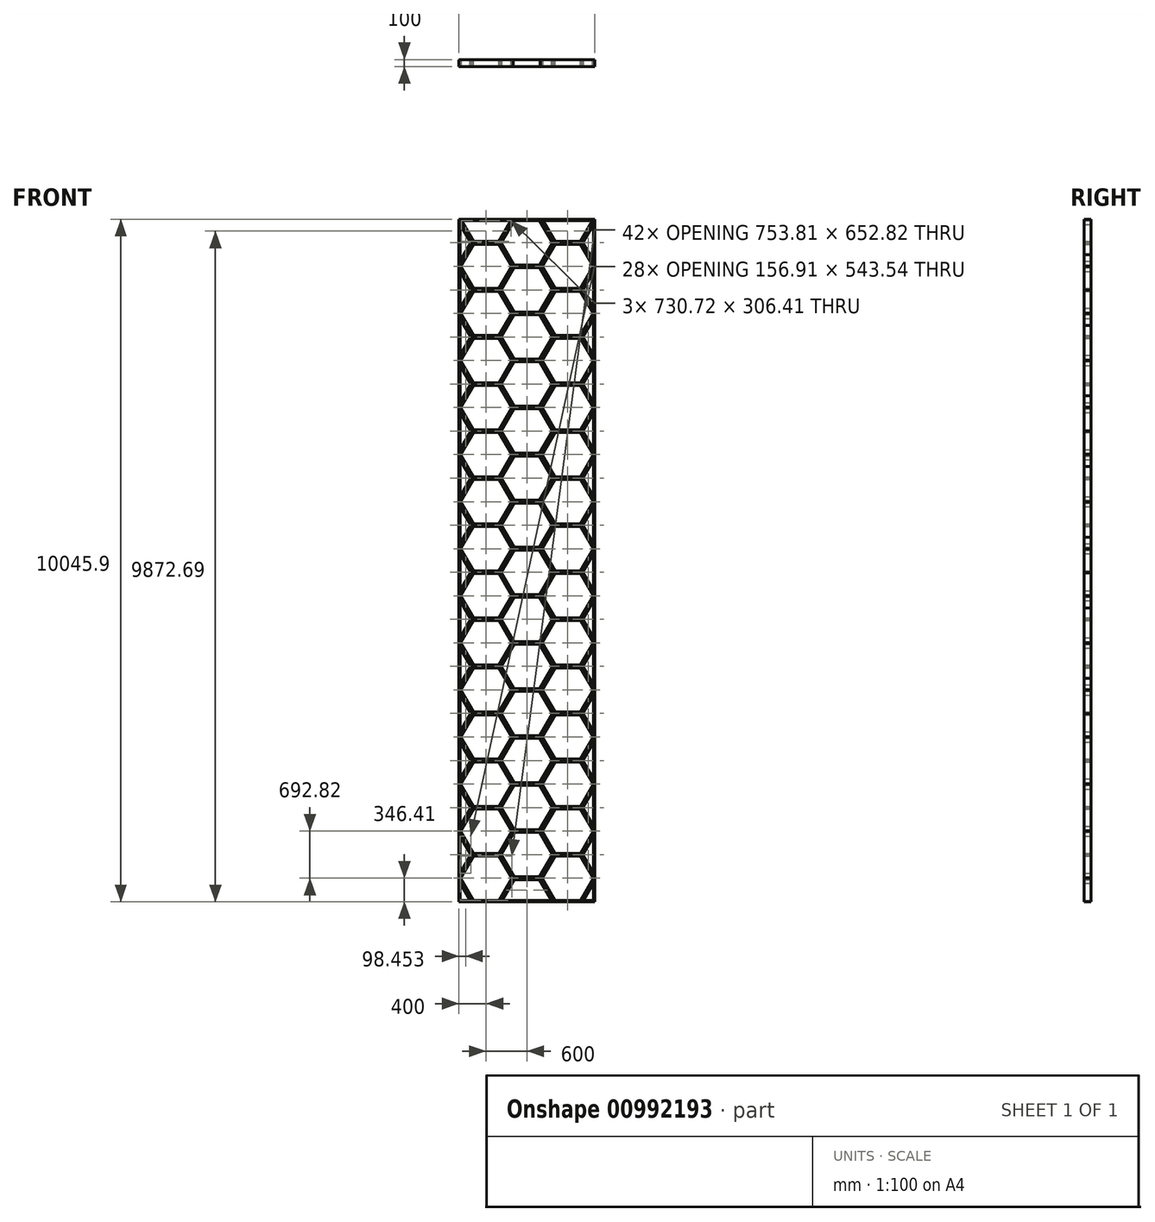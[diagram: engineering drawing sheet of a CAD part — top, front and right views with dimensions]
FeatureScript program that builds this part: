
annotation { "Feature Type Name" : "Feature", "Feature Type Description" : "" }
export const myFeature = defineFeature(function(context is Context, id is Id, definition is map)
    precondition{}
    {
        {
            var Q0;
            Q0=qCreatedBy(makeId("Front.planeOp"),FACE);
            var sketch = newSketch(context, id + "F0", { "sketchPlane" : qUnion([Q0])});
            skLineSegment(sketch, "E0", {"start": v(-200, 346.41) * mm, "end": v(200, 346.41) * mm});
            skLineSegment(sketch, "E1", {"start": v(200, 346.41) * mm, "end": v(400, 0) * mm});
            skLineSegment(sketch, "E2", {"start": v(400, 0) * mm, "end": v(200, -346.41) * mm});
            skLineSegment(sketch, "E3", {"start": v(200, -346.41) * mm, "end": v(-200, -346.41) * mm});
            skLineSegment(sketch, "E4", {"start": v(-200, -346.41) * mm, "end": v(-400, 0) * mm});
            skLineSegment(sketch, "E5", {"start": v(-400, 0) * mm, "end": v(-200, 346.41) * mm});
            skLineSegment(sketch, "E6", {"start": v(-400, 0) * mm, "end": v(-800, 0) * mm});
            skLineSegment(sketch, "E7", {"start": v(-800, 0) * mm, "end": v(-1000, -346.41) * mm});
            skLineSegment(sketch, "E8", {"start": v(-200, -346.41) * mm, "end": v(-1000, -346.41) * mm});
            skLineSegment(sketch, "E9", {"start": v(200, -346.41) * mm, "end": v(400, -346.41) * mm});
            skLineSegment(sketch, "E10", {"start": v(400, -346.41) * mm, "end": v(400, 0) * mm});
            skLineSegment(sketch, "E11", {"start": v(-1000, -346.41) * mm, "end": v(-1400, -346.41) * mm});
            skLineSegment(sketch, "E12", {"start": v(-1400, -346.41) * mm, "end": v(-1600, 0) * mm});
            skLineSegment(sketch, "E13", {"start": v(-1600, 0) * mm, "end": v(-1600, -346.41) * mm});
            skLineSegment(sketch, "E14", {"start": v(-1600, -346.41) * mm, "end": v(-1400, -346.41) * mm});
            skLineSegment(sketch, "E15", {"start": v(-1600, 0) * mm, "end": v(-1400, 346.41) * mm});
            skLineSegment(sketch, "E16", {"start": v(-1400, 346.41) * mm, "end": v(-1000, 346.41) * mm});
            skLineSegment(sketch, "E17", {"start": v(-1000, 346.41) * mm, "end": v(-800, 0) * mm});
            skLineSegment(sketch, "E18", {"start": v(-1400, 346.41) * mm, "end": v(-1600, 692.82) * mm});
            skLineSegment(sketch, "E19", {"start": v(-1600, 692.82) * mm, "end": v(-1600, 0) * mm});
            skLineSegment(sketch, "E20", {"start": v(-1600, 692.82) * mm, "end": v(-1400, 1039.23) * mm});
            skLineSegment(sketch, "E21", {"start": v(-1400, 1039.23) * mm, "end": v(-1000, 1039.23) * mm});
            skLineSegment(sketch, "E22", {"start": v(-1000, 1039.23) * mm, "end": v(-800, 692.82) * mm});
            skLineSegment(sketch, "E23", {"start": v(-800, 692.82) * mm, "end": v(-1000, 346.41) * mm});
            skLineSegment(sketch, "E24", {"start": v(-1400, 1039.23) * mm, "end": v(-1600, 1385.64) * mm});
            skLineSegment(sketch, "E25", {"start": v(-1600, 692.82) * mm, "end": v(-1600, 1385.64) * mm});
            skLineSegment(sketch, "E26", {"start": v(-1600, 1385.64) * mm, "end": v(-1400, 1732.05) * mm});
            skLineSegment(sketch, "E27", {"start": v(-1400, 1732.05) * mm, "end": v(-1600, 2078.46) * mm});
            skLineSegment(sketch, "E28", {"start": v(-1600, 2078.46) * mm, "end": v(-1600, 1385.64) * mm});
            skLineSegment(sketch, "E29", {"start": v(-1600, 2078.46) * mm, "end": v(-1400, 2424.87) * mm});
            skLineSegment(sketch, "E30", {"start": v(-1400, 2424.87) * mm, "end": v(-1600, 2771.28) * mm});
            skLineSegment(sketch, "E31", {"start": v(-1600, 2078.46) * mm, "end": v(-1600, 2771.28) * mm});
            skLineSegment(sketch, "E32.MirrorCS", {"start": v(-1600, 3464.1) * mm, "end": v(-1600, 2771.28) * mm});
            skLineSegment(sketch, "E33.MirrorCS", {"start": v(-1400, 4503.33) * mm, "end": v(-1600, 4156.92) * mm});
            skLineSegment(sketch, "E34.MirrorCS", {"start": v(-1600, 4849.74) * mm, "end": v(-1400, 4503.33) * mm});
            skLineSegment(sketch, "E35.MirrorCS", {"start": v(-1600, 3464.1) * mm, "end": v(-1400, 3117.7) * mm});
            skLineSegment(sketch, "E36.MirrorCS", {"start": v(-1400, 3810.51) * mm, "end": v(-1600, 3464.1) * mm});
            skLineSegment(sketch, "E37.MirrorCS", {"start": v(-1600, 4156.92) * mm, "end": v(-1400, 3810.51) * mm});
            skLineSegment(sketch, "E38.MirrorCS", {"start": v(-1400, 3117.7) * mm, "end": v(-1600, 2771.28) * mm});
            skLineSegment(sketch, "E39.MirrorCS", {"start": v(-1600, 3464.1) * mm, "end": v(-1600, 4156.92) * mm});
            skLineSegment(sketch, "E40", {"start": v(400, 0) * mm, "end": v(400, 9699.48) * mm});
            skLineSegment(sketch, "E41", {"start": v(-200, 346.41) * mm, "end": v(-400, 692.82) * mm});
            skLineSegment(sketch, "E42", {"start": v(-400, 692.82) * mm, "end": v(-800, 692.82) * mm});
            skLineSegment(sketch, "E43", {"start": v(200, 346.41) * mm, "end": v(400, 692.82) * mm});
            skLineSegment(sketch, "E44", {"start": v(400, 692.82) * mm, "end": v(200, 1039.23) * mm});
            skLineSegment(sketch, "E45", {"start": v(200, 1039.23) * mm, "end": v(-200, 1039.23) * mm});
            skLineSegment(sketch, "E46", {"start": v(-200, 1039.23) * mm, "end": v(-400, 692.82) * mm});
            skLineSegment(sketch, "E47", {"start": v(200, 1039.23) * mm, "end": v(400, 1385.64) * mm});
            skLineSegment(sketch, "E48", {"start": v(400, 1385.64) * mm, "end": v(200, 1732.05) * mm});
            skLineSegment(sketch, "E49", {"start": v(200, 1732.05) * mm, "end": v(-200, 1732.05) * mm});
            skLineSegment(sketch, "E50", {"start": v(-200, 1732.05) * mm, "end": v(-400, 1385.64) * mm});
            skLineSegment(sketch, "E51", {"start": v(-400, 1385.64) * mm, "end": v(-800, 1385.64) * mm});
            skLineSegment(sketch, "E52", {"start": v(-800, 1385.64) * mm, "end": v(-1000, 1039.23) * mm});
            skLineSegment(sketch, "E53", {"start": v(-200, 1039.23) * mm, "end": v(-400, 1385.64) * mm});
            skLineSegment(sketch, "E54", {"start": v(-1400, 1732.05) * mm, "end": v(-1000, 1732.05) * mm});
            skLineSegment(sketch, "E55", {"start": v(-1000, 1732.05) * mm, "end": v(-800, 1385.64) * mm});
            skLineSegment(sketch, "E56", {"start": v(400, 2078.46) * mm, "end": v(200, 1732.05) * mm});
            skLineSegment(sketch, "E57", {"start": v(-200, 1732.05) * mm, "end": v(-400, 2078.46) * mm});
            skLineSegment(sketch, "E58", {"start": v(-400, 2078.46) * mm, "end": v(-800, 2078.46) * mm});
            skLineSegment(sketch, "E59", {"start": v(-800, 2078.46) * mm, "end": v(-1000, 1732.05) * mm});
            skLineSegment(sketch, "E60", {"start": v(-1400, 2424.87) * mm, "end": v(-1000, 2424.87) * mm});
            skLineSegment(sketch, "E61", {"start": v(-1000, 2424.87) * mm, "end": v(-800, 2078.46) * mm});
            skLineSegment(sketch, "E62", {"start": v(-400, 2078.46) * mm, "end": v(-200, 2424.87) * mm});
            skLineSegment(sketch, "E63", {"start": v(-200, 2424.87) * mm, "end": v(200, 2424.87) * mm});
            skLineSegment(sketch, "E64", {"start": v(200, 2424.87) * mm, "end": v(400, 2078.46) * mm});
            skLineSegment(sketch, "E65", {"start": v(200, 2424.87) * mm, "end": v(400, 2771.28) * mm});
            skLineSegment(sketch, "E66", {"start": v(400, 2771.28) * mm, "end": v(200, 3117.7) * mm});
            skLineSegment(sketch, "E67", {"start": v(200, 3117.7) * mm, "end": v(400, 3464.1) * mm});
            skLineSegment(sketch, "E68", {"start": v(400, 3464.1) * mm, "end": v(200, 3810.51) * mm});
            skLineSegment(sketch, "E69", {"start": v(200, 3810.51) * mm, "end": v(400, 4156.92) * mm});
            skLineSegment(sketch, "E70", {"start": v(400, 4156.92) * mm, "end": v(200, 4503.33) * mm});
            skLineSegment(sketch, "E71", {"start": v(200, 4503.33) * mm, "end": v(400, 4849.74) * mm});
            skLineSegment(sketch, "E72", {"start": v(400, 4849.74) * mm, "end": v(200, 5196.15) * mm});
            skLineSegment(sketch, "E73", {"start": v(200, 5196.15) * mm, "end": v(400, 5542.56) * mm});
            skLineSegment(sketch, "E74", {"start": v(400, 5542.56) * mm, "end": v(200, 5888.97) * mm});
            skLineSegment(sketch, "E75", {"start": v(200, 5888.97) * mm, "end": v(400, 6235.38) * mm});
            skLineSegment(sketch, "E76", {"start": v(400, 6235.38) * mm, "end": v(200, 6581.8) * mm});
            skLineSegment(sketch, "E77", {"start": v(200, 6581.8) * mm, "end": v(400, 6928.2) * mm});
            skLineSegment(sketch, "E78", {"start": v(400, 6928.2) * mm, "end": v(200, 7274.61) * mm});
            skLineSegment(sketch, "E79", {"start": v(200, 7274.61) * mm, "end": v(400, 7621.02) * mm});
            skLineSegment(sketch, "E80", {"start": v(400, 7621.02) * mm, "end": v(200, 7967.43) * mm});
            skLineSegment(sketch, "E81", {"start": v(200, 7967.43) * mm, "end": v(400, 8313.84) * mm});
            skLineSegment(sketch, "E82", {"start": v(400, 8313.84) * mm, "end": v(200, 8660.25) * mm});
            skLineSegment(sketch, "E83", {"start": v(200, 8660.25) * mm, "end": v(400, 9006.66) * mm});
            skLineSegment(sketch, "E84", {"start": v(400, 9006.66) * mm, "end": v(200, 9353.07) * mm});
            skLineSegment(sketch, "E85", {"start": v(-1600, 4156.92) * mm, "end": v(-1600, 4849.74) * mm});
            skLineSegment(sketch, "E86", {"start": v(-1600, 4849.74) * mm, "end": v(-1600, 9699.48) * mm});
            skLineSegment(sketch, "E87", {"start": v(-1600, 4849.74) * mm, "end": v(-1400, 5196.15) * mm});
            skLineSegment(sketch, "E88", {"start": v(-1400, 5196.15) * mm, "end": v(-1600, 5542.56) * mm});
            skLineSegment(sketch, "E89", {"start": v(-1400, 5196.15) * mm, "end": v(-1000, 5196.15) * mm});
            skLineSegment(sketch, "E90", {"start": v(-1000, 5196.15) * mm, "end": v(-800, 4849.74) * mm});
            skLineSegment(sketch, "E91", {"start": v(-800, 4849.74) * mm, "end": v(-1000, 4503.33) * mm});
            skLineSegment(sketch, "E92", {"start": v(-1000, 4503.33) * mm, "end": v(-1400, 4503.33) * mm});
            skLineSegment(sketch, "E93", {"start": v(-1600, 5542.56) * mm, "end": v(-1400, 5888.97) * mm});
            skLineSegment(sketch, "E94", {"start": v(-1400, 5888.97) * mm, "end": v(-1600, 6235.38) * mm});
            skLineSegment(sketch, "E95", {"start": v(-1600, 6235.38) * mm, "end": v(-1400, 6581.8) * mm});
            skLineSegment(sketch, "E96", {"start": v(-1400, 6581.8) * mm, "end": v(-1600, 6928.2) * mm});
            skLineSegment(sketch, "E97", {"start": v(-1600, 6928.2) * mm, "end": v(-1400, 7274.61) * mm});
            skLineSegment(sketch, "E98", {"start": v(-1400, 7274.61) * mm, "end": v(-1600, 7621.02) * mm});
            skLineSegment(sketch, "E99", {"start": v(-1600, 7621.02) * mm, "end": v(-1400, 7967.43) * mm});
            skLineSegment(sketch, "E100", {"start": v(-1400, 7967.43) * mm, "end": v(-1600, 8313.84) * mm});
            skLineSegment(sketch, "E101", {"start": v(-1600, 8313.84) * mm, "end": v(-1400, 8660.25) * mm});
            skLineSegment(sketch, "E102", {"start": v(-1400, 8660.25) * mm, "end": v(-1600, 9006.66) * mm});
            skLineSegment(sketch, "E103", {"start": v(200, 9353.07) * mm, "end": v(400, 9699.48) * mm});
            skLineSegment(sketch, "E104", {"start": v(-1600, 9006.66) * mm, "end": v(-1400, 9353.07) * mm});
            skLineSegment(sketch, "E105", {"start": v(-1400, 9353.07) * mm, "end": v(-1600, 9699.48) * mm});
            skLineSegment(sketch, "E106", {"start": v(-1600, 9699.48) * mm, "end": v(400, 9699.48) * mm});
            skLineSegment(sketch, "E107", {"start": v(-200, 2424.87) * mm, "end": v(-400, 2771.28) * mm});
            skLineSegment(sketch, "E108", {"start": v(-400, 2771.28) * mm, "end": v(-200, 3117.7) * mm});
            skLineSegment(sketch, "E109", {"start": v(-200, 3117.7) * mm, "end": v(200, 3117.7) * mm});
            skLineSegment(sketch, "E110", {"start": v(-400, 2771.28) * mm, "end": v(-800, 2771.28) * mm});
            skLineSegment(sketch, "E111", {"start": v(-800, 2771.28) * mm, "end": v(-1000, 2424.87) * mm});
            skLineSegment(sketch, "E112", {"start": v(-1400, 3117.7) * mm, "end": v(-1000, 3117.7) * mm});
            skLineSegment(sketch, "E113", {"start": v(-1000, 3117.7) * mm, "end": v(-800, 2771.28) * mm});
            skLineSegment(sketch, "E114", {"start": v(-1400, 3810.51) * mm, "end": v(-1000, 3810.51) * mm});
            skLineSegment(sketch, "E115", {"start": v(-1000, 3810.51) * mm, "end": v(-800, 3464.1) * mm});
            skLineSegment(sketch, "E116", {"start": v(-800, 3464.1) * mm, "end": v(-1000, 3117.7) * mm});
            skLineSegment(sketch, "E117", {"start": v(-200, 3117.7) * mm, "end": v(-400, 3464.1) * mm});
            skLineSegment(sketch, "E118", {"start": v(-400, 3464.1) * mm, "end": v(-800, 3464.1) * mm});
            skLineSegment(sketch, "E119", {"start": v(-400, 3464.1) * mm, "end": v(-200, 3810.51) * mm});
            skLineSegment(sketch, "E120", {"start": v(-200, 3810.51) * mm, "end": v(200, 3810.51) * mm});
            skLineSegment(sketch, "E121", {"start": v(-1000, 3810.51) * mm, "end": v(-800, 4156.92) * mm});
            skLineSegment(sketch, "E122", {"start": v(-800, 4156.92) * mm, "end": v(-1000, 4503.33) * mm});
            skLineSegment(sketch, "E123", {"start": v(-800, 4849.74) * mm, "end": v(-400, 4849.74) * mm});
            skLineSegment(sketch, "E124", {"start": v(-400, 4849.74) * mm, "end": v(-200, 4503.33) * mm});
            skLineSegment(sketch, "E125", {"start": v(-200, 4503.33) * mm, "end": v(-400, 4156.92) * mm});
            skLineSegment(sketch, "E126", {"start": v(-400, 4156.92) * mm, "end": v(-800, 4156.92) * mm});
            skLineSegment(sketch, "E127", {"start": v(-400, 4156.92) * mm, "end": v(-200, 3810.51) * mm});
            skLineSegment(sketch, "E128", {"start": v(200, 4503.33) * mm, "end": v(-200, 4503.33) * mm});
            skLineSegment(sketch, "E129", {"start": v(-400, 4849.74) * mm, "end": v(-200, 5196.15) * mm});
            skLineSegment(sketch, "E130", {"start": v(-200, 5196.15) * mm, "end": v(200, 5196.15) * mm});
            skLineSegment(sketch, "E131", {"start": v(200, 5888.97) * mm, "end": v(-200, 5888.97) * mm});
            skLineSegment(sketch, "E132", {"start": v(-200, 5888.97) * mm, "end": v(-400, 5542.56) * mm});
            skLineSegment(sketch, "E133", {"start": v(-400, 5542.56) * mm, "end": v(-200, 5196.15) * mm});
            skLineSegment(sketch, "E134", {"start": v(-1000, 5196.15) * mm, "end": v(-800, 5542.56) * mm});
            skLineSegment(sketch, "E135", {"start": v(-800, 5542.56) * mm, "end": v(-400, 5542.56) * mm});
            skLineSegment(sketch, "E136", {"start": v(-1400, 5888.97) * mm, "end": v(-1000, 5888.97) * mm});
            skLineSegment(sketch, "E137", {"start": v(-1000, 5888.97) * mm, "end": v(-800, 5542.56) * mm});
            skLineSegment(sketch, "E138", {"start": v(-1000, 5888.97) * mm, "end": v(-800, 6235.38) * mm});
            skLineSegment(sketch, "E139", {"start": v(-800, 6235.38) * mm, "end": v(-400, 6235.38) * mm});
            skLineSegment(sketch, "E140", {"start": v(-400, 6235.38) * mm, "end": v(-200, 5888.97) * mm});
            skLineSegment(sketch, "E141", {"start": v(200, 6581.8) * mm, "end": v(-200, 6581.8) * mm});
            skLineSegment(sketch, "E142", {"start": v(-200, 6581.8) * mm, "end": v(-400, 6235.38) * mm});
            skLineSegment(sketch, "E143", {"start": v(-800, 6235.38) * mm, "end": v(-1000, 6581.8) * mm});
            skLineSegment(sketch, "E144", {"start": v(-1000, 6581.8) * mm, "end": v(-1400, 6581.8) * mm});
            skLineSegment(sketch, "E145", {"start": v(-1400, 7274.61) * mm, "end": v(-1000, 7274.61) * mm});
            skLineSegment(sketch, "E146", {"start": v(-1000, 7274.61) * mm, "end": v(-800, 6928.2) * mm});
            skLineSegment(sketch, "E147", {"start": v(-800, 6928.2) * mm, "end": v(-400, 6928.2) * mm});
            skLineSegment(sketch, "E148", {"start": v(-400, 6928.2) * mm, "end": v(-200, 7274.61) * mm});
            skLineSegment(sketch, "E149", {"start": v(-200, 7274.61) * mm, "end": v(200, 7274.61) * mm});
            skLineSegment(sketch, "E150", {"start": v(-400, 6928.2) * mm, "end": v(-200, 6581.8) * mm});
            skLineSegment(sketch, "E151", {"start": v(-800, 6928.2) * mm, "end": v(-1000, 6581.8) * mm});
            skLineSegment(sketch, "E152", {"start": v(-200, 7274.61) * mm, "end": v(-400, 7621.02) * mm});
            skLineSegment(sketch, "E153", {"start": v(-400, 7621.02) * mm, "end": v(-200, 7967.43) * mm});
            skLineSegment(sketch, "E154", {"start": v(-200, 7967.43) * mm, "end": v(200, 7967.43) * mm});
            skLineSegment(sketch, "E155", {"start": v(-400, 7621.02) * mm, "end": v(-800, 7621.02) * mm});
            skLineSegment(sketch, "E156", {"start": v(-800, 7621.02) * mm, "end": v(-1000, 7274.61) * mm});
            skLineSegment(sketch, "E157", {"start": v(-1400, 7967.43) * mm, "end": v(-1000, 7967.43) * mm});
            skLineSegment(sketch, "E158", {"start": v(-1000, 7967.43) * mm, "end": v(-800, 7621.02) * mm});
            skLineSegment(sketch, "E159", {"start": v(-1400, 8660.25) * mm, "end": v(-1000, 8660.25) * mm});
            skLineSegment(sketch, "E160", {"start": v(-1000, 8660.25) * mm, "end": v(-800, 8313.84) * mm});
            skLineSegment(sketch, "E161", {"start": v(-800, 8313.84) * mm, "end": v(-1000, 7967.43) * mm});
            skLineSegment(sketch, "E162", {"start": v(-200, 7967.43) * mm, "end": v(-400, 8313.84) * mm});
            skLineSegment(sketch, "E163", {"start": v(-400, 8313.84) * mm, "end": v(-800, 8313.84) * mm});
            skLineSegment(sketch, "E164", {"start": v(-400, 8313.84) * mm, "end": v(-200, 8660.25) * mm});
            skLineSegment(sketch, "E165", {"start": v(-200, 8660.25) * mm, "end": v(200, 8660.25) * mm});
            skLineSegment(sketch, "E166", {"start": v(-200, 8660.25) * mm, "end": v(-400, 9006.66) * mm});
            skLineSegment(sketch, "E167", {"start": v(-400, 9006.66) * mm, "end": v(-800, 9006.66) * mm});
            skLineSegment(sketch, "E168", {"start": v(-800, 9006.66) * mm, "end": v(-1000, 8660.25) * mm});
            skLineSegment(sketch, "E169", {"start": v(-1400, 9353.07) * mm, "end": v(-1000, 9353.07) * mm});
            skLineSegment(sketch, "E170", {"start": v(-1000, 9353.07) * mm, "end": v(-800, 9006.66) * mm});
            skLineSegment(sketch, "E171", {"start": v(-400, 9006.66) * mm, "end": v(-200, 9353.07) * mm});
            skLineSegment(sketch, "E172", {"start": v(-200, 9353.07) * mm, "end": v(200, 9353.07) * mm});
            skLineSegment(sketch, "E173", {"start": v(-200, 9353.07) * mm, "end": v(-400, 9699.48) * mm});
            skLineSegment(sketch, "E174", {"start": v(-1000, 9353.07) * mm, "end": v(-800, 9699.48) * mm});
            skPoint(sketch, "E175", {"position": v(400, 9179.48) * mm});
            skPoint(sketch, "E176", {"position": v(400, 8659.48) * mm});
            skPoint(sketch, "E177", {"position": v(400, 8139.48) * mm});
            skPoint(sketch, "E178", {"position": v(400, 7619.48) * mm});
            skPoint(sketch, "E179", {"position": v(400, 7099.48) * mm});
            skPoint(sketch, "E180", {"position": v(400, 6579.48) * mm});
            skPoint(sketch, "E181", {"position": v(400, 6059.48) * mm});
            skPoint(sketch, "E182", {"position": v(400, 5539.48) * mm});
            skPoint(sketch, "E183", {"position": v(400, 5019.48) * mm});
            skPoint(sketch, "E184", {"position": v(400, 4499.48) * mm});
            skPoint(sketch, "E185", {"position": v(400, 3979.48) * mm});
            skPoint(sketch, "E186", {"position": v(400, 3459.48) * mm});
            skPoint(sketch, "E187", {"position": v(400, 2939.48) * mm});
            skPoint(sketch, "E188", {"position": v(400, 2419.48) * mm});
            skPoint(sketch, "E189", {"position": v(400, 1899.48) * mm});
            skPoint(sketch, "E190", {"position": v(400, 1379.48) * mm});
            skPoint(sketch, "E191", {"position": v(400, -173.2) * mm});
            skPoint(sketch, "E192", {"position": v(400, 859.48) * mm});
            skPoint(sketch, "E193", {"position": v(400, 339.48) * mm});
            skSolve(sketch);
        }
        {
            var Q0;
            Q0=makeQuery(id+"F0.imprint","IMPRINT",FACE,{"disambiguationData":[TD([[makeQuery(id+"F0.imprint","IMPRINT",EDGE,{"derivedFrom":sQuery(id+"F0.wireOp",EDGE,"E153")}),1.0]])]});
            var Q1;
            Q1=makeQuery(id+"F0.imprint","IMPRINT",FACE,{"disambiguationData":[TD([[makeQuery(id+"F0.imprint","IMPRINT",EDGE,{"derivedFrom":sQuery(id+"F0.wireOp",EDGE,"E22")}),1.0]])]});
            var Q2;
            Q2=makeQuery(id+"F0.imprint","IMPRINT",FACE,{"disambiguationData":[TD([[makeQuery(id+"F0.imprint","IMPRINT",EDGE,{"derivedFrom":sQuery(id+"F0.wireOp",EDGE,"E58")}),-1.0]])]});
            var Q3;
            Q3=makeQuery(id+"F0.imprint","IMPRINT",FACE,{"disambiguationData":[TD([[makeQuery(id+"F0.imprint","IMPRINT",EDGE,{"derivedFrom":sQuery(id+"F0.wireOp",EDGE,"E115")}),1.0]])]});
            var Q4;
            Q4=makeQuery(id+"F0.imprint","IMPRINT",FACE,{"disambiguationData":[TD([[makeQuery(id+"F0.imprint","IMPRINT",EDGE,{"derivedFrom":sQuery(id+"F0.wireOp",EDGE,"E90")}),1.0]])]});
            var Q5;
            Q5=makeQuery(id+"F0.imprint","IMPRINT",FACE,{"disambiguationData":[TD([[makeQuery(id+"F0.imprint","IMPRINT",EDGE,{"derivedFrom":sQuery(id+"F0.wireOp",EDGE,"E139")}),1.0]])]});
            var Q6;
            Q6=makeQuery(id+"F0.imprint","IMPRINT",FACE,{"disambiguationData":[TD([[makeQuery(id+"F0.imprint","IMPRINT",EDGE,{"derivedFrom":sQuery(id+"F0.wireOp",EDGE,"E2")}),1.0]])]});
            var Q7;
            Q7=makeQuery(id+"F0.imprint","IMPRINT",FACE,{"disambiguationData":[TD([[makeQuery(id+"F0.imprint","IMPRINT",EDGE,{"derivedFrom":sQuery(id+"F0.wireOp",EDGE,"E12")}),1.0]])]});
            var Q8;
            {var subQ0=sQuery(id+"F0.wireOp",EDGE,"E1");Q8=makeQuery(id+"F0.imprint","IMPRINT",FACE,{"disambiguationData":[TD([[makeQuery(id+"F0.imprint","IMPRINT",EDGE,{"derivedFrom":subQ0}),1.0]])]});}
            var Q9;
            Q9=makeQuery(id+"F0.imprint","IMPRINT",FACE,{"disambiguationData":[TD([[makeQuery(id+"F0.imprint","IMPRINT",EDGE,{"derivedFrom":sQuery(id+"F0.wireOp",EDGE,"E15")}),1.0]])]});
            var Q10;
            Q10=makeQuery(id+"F0.imprint","IMPRINT",FACE,{"disambiguationData":[TD([[makeQuery(id+"F0.imprint","IMPRINT",EDGE,{"derivedFrom":sQuery(id+"F0.wireOp",EDGE,"E20")}),1.0]])]});
            var Q11;
            Q11=makeQuery(id+"F0.imprint","IMPRINT",FACE,{"disambiguationData":[TD([[makeQuery(id+"F0.imprint","IMPRINT",EDGE,{"derivedFrom":sQuery(id+"F0.wireOp",EDGE,"E26")}),1.0]])]});
            var Q12;
            Q12=makeQuery(id+"F0.imprint","IMPRINT",FACE,{"disambiguationData":[TD([[makeQuery(id+"F0.imprint","IMPRINT",EDGE,{"derivedFrom":sQuery(id+"F0.wireOp",EDGE,"E29")}),1.0]])]});
            var Q13;
            Q13=makeQuery(id+"F0.imprint","IMPRINT",FACE,{"disambiguationData":[TD([[makeQuery(id+"F0.imprint","IMPRINT",EDGE,{"derivedFrom":sQuery(id+"F0.wireOp",EDGE,"E32.MirrorCS")}),1.0]])]});
            var Q14;
            Q14=makeQuery(id+"F0.imprint","IMPRINT",FACE,{"disambiguationData":[TD([[makeQuery(id+"F0.imprint","IMPRINT",EDGE,{"derivedFrom":sQuery(id+"F0.wireOp",EDGE,"E33.MirrorCS")}),-1.0]])]});
            var Q15;
            Q15=makeQuery(id+"F0.imprint","IMPRINT",FACE,{"disambiguationData":[TD([[makeQuery(id+"F0.imprint","IMPRINT",EDGE,{"derivedFrom":sQuery(id+"F0.wireOp",EDGE,"E36.MirrorCS")}),-1.0]])]});
            var Q16;
            {var subQ0=sQuery(id+"F0.wireOp",EDGE,"E44");Q16=makeQuery(id+"F0.imprint","IMPRINT",FACE,{"disambiguationData":[TD([[makeQuery(id+"F0.imprint","IMPRINT",EDGE,{"derivedFrom":subQ0}),-1.0]])]});}
            var Q17;
            {var subQ0=sQuery(id+"F0.wireOp",EDGE,"E48");Q17=makeQuery(id+"F0.imprint","IMPRINT",FACE,{"disambiguationData":[TD([[makeQuery(id+"F0.imprint","IMPRINT",EDGE,{"derivedFrom":subQ0}),-1.0]])]});}
            var Q18;
            {var subQ0=sQuery(id+"F0.wireOp",EDGE,"E64");Q18=makeQuery(id+"F0.imprint","IMPRINT",FACE,{"disambiguationData":[TD([[makeQuery(id+"F0.imprint","IMPRINT",EDGE,{"derivedFrom":subQ0}),1.0]])]});}
            var Q19;
            {var subQ0=sQuery(id+"F0.wireOp",EDGE,"E66");Q19=makeQuery(id+"F0.imprint","IMPRINT",FACE,{"disambiguationData":[TD([[makeQuery(id+"F0.imprint","IMPRINT",EDGE,{"derivedFrom":subQ0}),-1.0]])]});}
            var Q20;
            {var subQ0=sQuery(id+"F0.wireOp",EDGE,"E68");Q20=makeQuery(id+"F0.imprint","IMPRINT",FACE,{"disambiguationData":[TD([[makeQuery(id+"F0.imprint","IMPRINT",EDGE,{"derivedFrom":subQ0}),-1.0]])]});}
            var Q21;
            {var subQ0=sQuery(id+"F0.wireOp",EDGE,"E70");Q21=makeQuery(id+"F0.imprint","IMPRINT",FACE,{"disambiguationData":[TD([[makeQuery(id+"F0.imprint","IMPRINT",EDGE,{"derivedFrom":subQ0}),-1.0]])]});}
            var Q22;
            {var subQ0=sQuery(id+"F0.wireOp",EDGE,"E72");Q22=makeQuery(id+"F0.imprint","IMPRINT",FACE,{"disambiguationData":[TD([[makeQuery(id+"F0.imprint","IMPRINT",EDGE,{"derivedFrom":subQ0}),-1.0]])]});}
            var Q23;
            {var subQ0=sQuery(id+"F0.wireOp",EDGE,"E74");Q23=makeQuery(id+"F0.imprint","IMPRINT",FACE,{"disambiguationData":[TD([[makeQuery(id+"F0.imprint","IMPRINT",EDGE,{"derivedFrom":subQ0}),-1.0]])]});}
            var Q24;
            {var subQ0=sQuery(id+"F0.wireOp",EDGE,"E76");Q24=makeQuery(id+"F0.imprint","IMPRINT",FACE,{"disambiguationData":[TD([[makeQuery(id+"F0.imprint","IMPRINT",EDGE,{"derivedFrom":subQ0}),-1.0]])]});}
            var Q25;
            {var subQ0=sQuery(id+"F0.wireOp",EDGE,"E78");Q25=makeQuery(id+"F0.imprint","IMPRINT",FACE,{"disambiguationData":[TD([[makeQuery(id+"F0.imprint","IMPRINT",EDGE,{"derivedFrom":subQ0}),-1.0]])]});}
            var Q26;
            {var subQ0=sQuery(id+"F0.wireOp",EDGE,"E80");Q26=makeQuery(id+"F0.imprint","IMPRINT",FACE,{"disambiguationData":[TD([[makeQuery(id+"F0.imprint","IMPRINT",EDGE,{"derivedFrom":subQ0}),-1.0]])]});}
            var Q27;
            {var subQ0=sQuery(id+"F0.wireOp",EDGE,"E82");Q27=makeQuery(id+"F0.imprint","IMPRINT",FACE,{"disambiguationData":[TD([[makeQuery(id+"F0.imprint","IMPRINT",EDGE,{"derivedFrom":subQ0}),-1.0]])]});}
            var Q28;
            {var subQ2=sQuery(id+"F0.wireOp",EDGE,"E84");Q28=makeQuery(id+"F0.imprint","IMPRINT",FACE,{"disambiguationData":[TD([[makeQuery(id+"F0.imprint","IMPRINT",EDGE,{"derivedFrom":subQ2}),-1.0]])]});}
            var Q29;
            {var subQ0=sQuery(id+"F0.wireOp",EDGE,"E87");Q29=makeQuery(id+"F0.imprint","IMPRINT",FACE,{"disambiguationData":[TD([[makeQuery(id+"F0.imprint","IMPRINT",EDGE,{"derivedFrom":subQ0}),1.0]])]});}
            var Q30;
            {var subQ0=sQuery(id+"F0.wireOp",EDGE,"E93");Q30=makeQuery(id+"F0.imprint","IMPRINT",FACE,{"disambiguationData":[TD([[makeQuery(id+"F0.imprint","IMPRINT",EDGE,{"derivedFrom":subQ0}),1.0]])]});}
            var Q31;
            {var subQ0=sQuery(id+"F0.wireOp",EDGE,"E95");Q31=makeQuery(id+"F0.imprint","IMPRINT",FACE,{"disambiguationData":[TD([[makeQuery(id+"F0.imprint","IMPRINT",EDGE,{"derivedFrom":subQ0}),1.0]])]});}
            var Q32;
            {var subQ0=sQuery(id+"F0.wireOp",EDGE,"E97");Q32=makeQuery(id+"F0.imprint","IMPRINT",FACE,{"disambiguationData":[TD([[makeQuery(id+"F0.imprint","IMPRINT",EDGE,{"derivedFrom":subQ0}),1.0]])]});}
            var Q33;
            {var subQ0=sQuery(id+"F0.wireOp",EDGE,"E99");Q33=makeQuery(id+"F0.imprint","IMPRINT",FACE,{"disambiguationData":[TD([[makeQuery(id+"F0.imprint","IMPRINT",EDGE,{"derivedFrom":subQ0}),1.0]])]});}
            var Q34;
            {var subQ0=sQuery(id+"F0.wireOp",EDGE,"E101");Q34=makeQuery(id+"F0.imprint","IMPRINT",FACE,{"disambiguationData":[TD([[makeQuery(id+"F0.imprint","IMPRINT",EDGE,{"derivedFrom":subQ0}),1.0]])]});}
            var Q35;
            {var subQ2=sQuery(id+"F0.wireOp",EDGE,"E104");Q35=makeQuery(id+"F0.imprint","IMPRINT",FACE,{"disambiguationData":[TD([[makeQuery(id+"F0.imprint","IMPRINT",EDGE,{"derivedFrom":subQ2}),1.0]])]});}
            var Q36;
            Q36=makeQuery(id+"F0.imprint","IMPRINT",FACE,{"disambiguationData":[TD([[makeQuery(id+"F0.imprint","IMPRINT",EDGE,{"derivedFrom":sQuery(id+"F0.wireOp",EDGE,"E4")}),1.0]])]});
            var Q37;
            Q37=makeQuery(id+"F0.imprint","IMPRINT",FACE,{"disambiguationData":[TD([[makeQuery(id+"F0.imprint","IMPRINT",EDGE,{"derivedFrom":sQuery(id+"F0.wireOp",EDGE,"E167")}),-1.0]])]});
            extrude(context, id + "F1", {"entities" : qUnion([Q0, Q1, Q2, Q3, Q4, Q5, Q6, Q7, Q8, Q9, Q10, Q11, Q12, Q13, Q14, Q15, Q16, Q17, Q18, Q19, Q20, Q21, Q22, Q23, Q24, Q25, Q26, Q27, Q28, Q29, Q30, Q31, Q32, Q33, Q34, Q35, Q36, Q37]), "depth" : 100 * mm, "offsetDistance" : 25 * mm});
        }
        {
            var Q0;
            Q0=makeQuery(id+"F1.opExtrude","CAP_FACE",FACE,{"disambiguationData":[OSD([sQuery(id+"F0.wireOp",EDGE,"E106"),sQuery(id+"F0.wireOp",EDGE,"E167"),sQuery(id+"F0.wireOp",EDGE,"E170"),sQuery(id+"F0.wireOp",EDGE,"E171"),sQuery(id+"F0.wireOp",EDGE,"E173"),sQuery(id+"F0.wireOp",EDGE,"E174")])],"isStart":false});
            var Q1;
            Q1=makeQuery(id+"F1.opExtrude","CAP_FACE",FACE,{"disambiguationData":[OSD([sQuery(id+"F0.wireOp",EDGE,"E86"),sQuery(id+"F0.wireOp",EDGE,"E104"),sQuery(id+"F0.wireOp",EDGE,"E105")])],"isStart":false});
            var Q2;
            Q2=makeQuery(id+"F1.opExtrude","CAP_FACE",FACE,{"disambiguationData":[OSD([sQuery(id+"F0.wireOp",EDGE,"E86"),sQuery(id+"F0.wireOp",EDGE,"E101"),sQuery(id+"F0.wireOp",EDGE,"E102")])],"isStart":false});
            var Q3;
            Q3=makeQuery(id+"F1.opExtrude","CAP_FACE",FACE,{"disambiguationData":[OSD([sQuery(id+"F0.wireOp",EDGE,"E86"),sQuery(id+"F0.wireOp",EDGE,"E99"),sQuery(id+"F0.wireOp",EDGE,"E100")])],"isStart":false});
            var Q4;
            Q4=makeQuery(id+"F1.opExtrude","CAP_FACE",FACE,{"disambiguationData":[OSD([sQuery(id+"F0.wireOp",EDGE,"E86"),sQuery(id+"F0.wireOp",EDGE,"E97"),sQuery(id+"F0.wireOp",EDGE,"E98")])],"isStart":false});
            var Q5;
            Q5=makeQuery(id+"F1.opExtrude","CAP_FACE",FACE,{"disambiguationData":[OSD([sQuery(id+"F0.wireOp",EDGE,"E86"),sQuery(id+"F0.wireOp",EDGE,"E95"),sQuery(id+"F0.wireOp",EDGE,"E96")])],"isStart":false});
            var Q6;
            Q6=makeQuery(id+"F1.opExtrude","CAP_FACE",FACE,{"disambiguationData":[OSD([sQuery(id+"F0.wireOp",EDGE,"E86"),sQuery(id+"F0.wireOp",EDGE,"E93"),sQuery(id+"F0.wireOp",EDGE,"E94")])],"isStart":false});
            var Q7;
            Q7=makeQuery(id+"F1.opExtrude","CAP_FACE",FACE,{"disambiguationData":[OSD([sQuery(id+"F0.wireOp",EDGE,"E86"),sQuery(id+"F0.wireOp",EDGE,"E87"),sQuery(id+"F0.wireOp",EDGE,"E88")])],"isStart":false});
            var Q8;
            Q8=makeQuery(id+"F1.opExtrude","CAP_FACE",FACE,{"disambiguationData":[OSD([sQuery(id+"F0.wireOp",EDGE,"E33.MirrorCS"),sQuery(id+"F0.wireOp",EDGE,"E34.MirrorCS"),sQuery(id+"F0.wireOp",EDGE,"E85")])],"isStart":false});
            var Q9;
            Q9=makeQuery(id+"F1.opExtrude","CAP_FACE",FACE,{"disambiguationData":[OSD([sQuery(id+"F0.wireOp",EDGE,"E36.MirrorCS"),sQuery(id+"F0.wireOp",EDGE,"E37.MirrorCS"),sQuery(id+"F0.wireOp",EDGE,"E39.MirrorCS")])],"isStart":false});
            var Q10;
            Q10=makeQuery(id+"F1.opExtrude","CAP_FACE",FACE,{"disambiguationData":[OSD([sQuery(id+"F0.wireOp",EDGE,"E32.MirrorCS"),sQuery(id+"F0.wireOp",EDGE,"E35.MirrorCS"),sQuery(id+"F0.wireOp",EDGE,"E38.MirrorCS")])],"isStart":false});
            var Q11;
            Q11=makeQuery(id+"F1.opExtrude","CAP_FACE",FACE,{"disambiguationData":[OSD([sQuery(id+"F0.wireOp",EDGE,"E29"),sQuery(id+"F0.wireOp",EDGE,"E30"),sQuery(id+"F0.wireOp",EDGE,"E31")])],"isStart":false});
            var Q12;
            Q12=makeQuery(id+"F1.opExtrude","CAP_FACE",FACE,{"disambiguationData":[OSD([sQuery(id+"F0.wireOp",EDGE,"E26"),sQuery(id+"F0.wireOp",EDGE,"E27"),sQuery(id+"F0.wireOp",EDGE,"E28")])],"isStart":false});
            var Q13;
            Q13=makeQuery(id+"F1.opExtrude","CAP_FACE",FACE,{"disambiguationData":[OSD([sQuery(id+"F0.wireOp",EDGE,"E20"),sQuery(id+"F0.wireOp",EDGE,"E24"),sQuery(id+"F0.wireOp",EDGE,"E25")])],"isStart":false});
            var Q14;
            Q14=makeQuery(id+"F1.opExtrude","CAP_FACE",FACE,{"disambiguationData":[OSD([sQuery(id+"F0.wireOp",EDGE,"E15"),sQuery(id+"F0.wireOp",EDGE,"E18"),sQuery(id+"F0.wireOp",EDGE,"E19")])],"isStart":false});
            var Q15;
            Q15=makeQuery(id+"F1.opExtrude","CAP_FACE",FACE,{"disambiguationData":[OSD([sQuery(id+"F0.wireOp",EDGE,"E12"),sQuery(id+"F0.wireOp",EDGE,"E13"),sQuery(id+"F0.wireOp",EDGE,"E14")])],"isStart":false});
            var Q16;
            Q16=makeQuery(id+"F1.opExtrude","CAP_FACE",FACE,{"disambiguationData":[OSD([sQuery(id+"F0.wireOp",EDGE,"E4"),sQuery(id+"F0.wireOp",EDGE,"E6"),sQuery(id+"F0.wireOp",EDGE,"E7"),sQuery(id+"F0.wireOp",EDGE,"E8")])],"isStart":false});
            var Q17;
            Q17=makeQuery(id+"F1.opExtrude","CAP_FACE",FACE,{"disambiguationData":[OSD([sQuery(id+"F0.wireOp",EDGE,"E2"),sQuery(id+"F0.wireOp",EDGE,"E9"),sQuery(id+"F0.wireOp",EDGE,"E10")])],"isStart":false});
            var Q18;
            Q18=makeQuery(id+"F1.opExtrude","CAP_FACE",FACE,{"disambiguationData":[OSD([sQuery(id+"F0.wireOp",EDGE,"E1"),sQuery(id+"F0.wireOp",EDGE,"E40"),sQuery(id+"F0.wireOp",EDGE,"E43")])],"isStart":false});
            var Q19;
            Q19=makeQuery(id+"F1.opExtrude","CAP_FACE",FACE,{"disambiguationData":[OSD([sQuery(id+"F0.wireOp",EDGE,"E40"),sQuery(id+"F0.wireOp",EDGE,"E44"),sQuery(id+"F0.wireOp",EDGE,"E47")])],"isStart":false});
            var Q20;
            Q20=makeQuery(id+"F1.opExtrude","CAP_FACE",FACE,{"disambiguationData":[OSD([sQuery(id+"F0.wireOp",EDGE,"E40"),sQuery(id+"F0.wireOp",EDGE,"E48"),sQuery(id+"F0.wireOp",EDGE,"E56")])],"isStart":false});
            var Q21;
            Q21=makeQuery(id+"F1.opExtrude","CAP_FACE",FACE,{"disambiguationData":[OSD([sQuery(id+"F0.wireOp",EDGE,"E22"),sQuery(id+"F0.wireOp",EDGE,"E42"),sQuery(id+"F0.wireOp",EDGE,"E46"),sQuery(id+"F0.wireOp",EDGE,"E51"),sQuery(id+"F0.wireOp",EDGE,"E52"),sQuery(id+"F0.wireOp",EDGE,"E53")])],"isStart":false});
            var Q22;
            Q22=makeQuery(id+"F1.opExtrude","CAP_FACE",FACE,{"disambiguationData":[OSD([sQuery(id+"F0.wireOp",EDGE,"E58"),sQuery(id+"F0.wireOp",EDGE,"E61"),sQuery(id+"F0.wireOp",EDGE,"E62"),sQuery(id+"F0.wireOp",EDGE,"E107"),sQuery(id+"F0.wireOp",EDGE,"E110"),sQuery(id+"F0.wireOp",EDGE,"E111")])],"isStart":false});
            var Q23;
            Q23=makeQuery(id+"F1.opExtrude","CAP_FACE",FACE,{"disambiguationData":[OSD([sQuery(id+"F0.wireOp",EDGE,"E115"),sQuery(id+"F0.wireOp",EDGE,"E118"),sQuery(id+"F0.wireOp",EDGE,"E119"),sQuery(id+"F0.wireOp",EDGE,"E121"),sQuery(id+"F0.wireOp",EDGE,"E126"),sQuery(id+"F0.wireOp",EDGE,"E127")])],"isStart":false});
            var Q24;
            Q24=makeQuery(id+"F1.opExtrude","CAP_FACE",FACE,{"disambiguationData":[OSD([sQuery(id+"F0.wireOp",EDGE,"E90"),sQuery(id+"F0.wireOp",EDGE,"E123"),sQuery(id+"F0.wireOp",EDGE,"E129"),sQuery(id+"F0.wireOp",EDGE,"E133"),sQuery(id+"F0.wireOp",EDGE,"E134"),sQuery(id+"F0.wireOp",EDGE,"E135")])],"isStart":false});
            var Q25;
            Q25=makeQuery(id+"F1.opExtrude","CAP_FACE",FACE,{"disambiguationData":[OSD([sQuery(id+"F0.wireOp",EDGE,"E139"),sQuery(id+"F0.wireOp",EDGE,"E142"),sQuery(id+"F0.wireOp",EDGE,"E143"),sQuery(id+"F0.wireOp",EDGE,"E147"),sQuery(id+"F0.wireOp",EDGE,"E150"),sQuery(id+"F0.wireOp",EDGE,"E151")])],"isStart":false});
            var Q26;
            Q26=makeQuery(id+"F1.opExtrude","CAP_FACE",FACE,{"disambiguationData":[OSD([sQuery(id+"F0.wireOp",EDGE,"E153"),sQuery(id+"F0.wireOp",EDGE,"E155"),sQuery(id+"F0.wireOp",EDGE,"E158"),sQuery(id+"F0.wireOp",EDGE,"E161"),sQuery(id+"F0.wireOp",EDGE,"E162"),sQuery(id+"F0.wireOp",EDGE,"E163")])],"isStart":false});
            var Q27;
            Q27=makeQuery(id+"F1.opExtrude","CAP_FACE",FACE,{"disambiguationData":[OSD([sQuery(id+"F0.wireOp",EDGE,"E40"),sQuery(id+"F0.wireOp",EDGE,"E64"),sQuery(id+"F0.wireOp",EDGE,"E65")])],"isStart":false});
            var Q28;
            Q28=makeQuery(id+"F1.opExtrude","CAP_FACE",FACE,{"disambiguationData":[OSD([sQuery(id+"F0.wireOp",EDGE,"E40"),sQuery(id+"F0.wireOp",EDGE,"E66"),sQuery(id+"F0.wireOp",EDGE,"E67")])],"isStart":false});
            var Q29;
            Q29=makeQuery(id+"F1.opExtrude","CAP_FACE",FACE,{"disambiguationData":[OSD([sQuery(id+"F0.wireOp",EDGE,"E40"),sQuery(id+"F0.wireOp",EDGE,"E68"),sQuery(id+"F0.wireOp",EDGE,"E69")])],"isStart":false});
            var Q30;
            Q30=makeQuery(id+"F1.opExtrude","CAP_FACE",FACE,{"disambiguationData":[OSD([sQuery(id+"F0.wireOp",EDGE,"E40"),sQuery(id+"F0.wireOp",EDGE,"E70"),sQuery(id+"F0.wireOp",EDGE,"E71")])],"isStart":false});
            var Q31;
            Q31=makeQuery(id+"F1.opExtrude","CAP_FACE",FACE,{"disambiguationData":[OSD([sQuery(id+"F0.wireOp",EDGE,"E40"),sQuery(id+"F0.wireOp",EDGE,"E72"),sQuery(id+"F0.wireOp",EDGE,"E73")])],"isStart":false});
            var Q32;
            Q32=makeQuery(id+"F1.opExtrude","CAP_FACE",FACE,{"disambiguationData":[OSD([sQuery(id+"F0.wireOp",EDGE,"E40"),sQuery(id+"F0.wireOp",EDGE,"E74"),sQuery(id+"F0.wireOp",EDGE,"E75")])],"isStart":false});
            var Q33;
            Q33=makeQuery(id+"F1.opExtrude","CAP_FACE",FACE,{"disambiguationData":[OSD([sQuery(id+"F0.wireOp",EDGE,"E40"),sQuery(id+"F0.wireOp",EDGE,"E76"),sQuery(id+"F0.wireOp",EDGE,"E77")])],"isStart":false});
            var Q34;
            Q34=makeQuery(id+"F1.opExtrude","CAP_FACE",FACE,{"disambiguationData":[OSD([sQuery(id+"F0.wireOp",EDGE,"E40"),sQuery(id+"F0.wireOp",EDGE,"E78"),sQuery(id+"F0.wireOp",EDGE,"E79")])],"isStart":false});
            var Q35;
            Q35=makeQuery(id+"F1.opExtrude","CAP_FACE",FACE,{"disambiguationData":[OSD([sQuery(id+"F0.wireOp",EDGE,"E40"),sQuery(id+"F0.wireOp",EDGE,"E80"),sQuery(id+"F0.wireOp",EDGE,"E81")])],"isStart":false});
            var Q36;
            Q36=makeQuery(id+"F1.opExtrude","CAP_FACE",FACE,{"disambiguationData":[OSD([sQuery(id+"F0.wireOp",EDGE,"E40"),sQuery(id+"F0.wireOp",EDGE,"E82"),sQuery(id+"F0.wireOp",EDGE,"E83")])],"isStart":false});
            var Q37;
            Q37=makeQuery(id+"F1.opExtrude","CAP_FACE",FACE,{"disambiguationData":[OSD([sQuery(id+"F0.wireOp",EDGE,"E40"),sQuery(id+"F0.wireOp",EDGE,"E84"),sQuery(id+"F0.wireOp",EDGE,"E103")])],"isStart":false});
            var Q38;
            Q38=makeQuery(id+"F1.opExtrude","CAP_FACE",FACE,{"disambiguationData":[OSD([sQuery(id+"F0.wireOp",EDGE,"E106"),sQuery(id+"F0.wireOp",EDGE,"E167"),sQuery(id+"F0.wireOp",EDGE,"E170"),sQuery(id+"F0.wireOp",EDGE,"E171"),sQuery(id+"F0.wireOp",EDGE,"E173"),sQuery(id+"F0.wireOp",EDGE,"E174")])],"isStart":true});
            var Q39;
            Q39=makeQuery(id+"F1.opExtrude","CAP_FACE",FACE,{"disambiguationData":[OSD([sQuery(id+"F0.wireOp",EDGE,"E153"),sQuery(id+"F0.wireOp",EDGE,"E155"),sQuery(id+"F0.wireOp",EDGE,"E158"),sQuery(id+"F0.wireOp",EDGE,"E161"),sQuery(id+"F0.wireOp",EDGE,"E162"),sQuery(id+"F0.wireOp",EDGE,"E163")])],"isStart":true});
            var Q40;
            Q40=makeQuery(id+"F1.opExtrude","CAP_FACE",FACE,{"disambiguationData":[OSD([sQuery(id+"F0.wireOp",EDGE,"E139"),sQuery(id+"F0.wireOp",EDGE,"E142"),sQuery(id+"F0.wireOp",EDGE,"E143"),sQuery(id+"F0.wireOp",EDGE,"E147"),sQuery(id+"F0.wireOp",EDGE,"E150"),sQuery(id+"F0.wireOp",EDGE,"E151")])],"isStart":true});
            var Q41;
            Q41=makeQuery(id+"F1.opExtrude","CAP_FACE",FACE,{"disambiguationData":[OSD([sQuery(id+"F0.wireOp",EDGE,"E90"),sQuery(id+"F0.wireOp",EDGE,"E123"),sQuery(id+"F0.wireOp",EDGE,"E129"),sQuery(id+"F0.wireOp",EDGE,"E133"),sQuery(id+"F0.wireOp",EDGE,"E134"),sQuery(id+"F0.wireOp",EDGE,"E135")])],"isStart":true});
            var Q42;
            Q42=makeQuery(id+"F1.opExtrude","CAP_FACE",FACE,{"disambiguationData":[OSD([sQuery(id+"F0.wireOp",EDGE,"E115"),sQuery(id+"F0.wireOp",EDGE,"E118"),sQuery(id+"F0.wireOp",EDGE,"E119"),sQuery(id+"F0.wireOp",EDGE,"E121"),sQuery(id+"F0.wireOp",EDGE,"E126"),sQuery(id+"F0.wireOp",EDGE,"E127")])],"isStart":true});
            var Q43;
            Q43=makeQuery(id+"F1.opExtrude","CAP_FACE",FACE,{"disambiguationData":[OSD([sQuery(id+"F0.wireOp",EDGE,"E58"),sQuery(id+"F0.wireOp",EDGE,"E61"),sQuery(id+"F0.wireOp",EDGE,"E62"),sQuery(id+"F0.wireOp",EDGE,"E107"),sQuery(id+"F0.wireOp",EDGE,"E110"),sQuery(id+"F0.wireOp",EDGE,"E111")])],"isStart":true});
            var Q44;
            Q44=makeQuery(id+"F1.opExtrude","CAP_FACE",FACE,{"disambiguationData":[OSD([sQuery(id+"F0.wireOp",EDGE,"E22"),sQuery(id+"F0.wireOp",EDGE,"E42"),sQuery(id+"F0.wireOp",EDGE,"E46"),sQuery(id+"F0.wireOp",EDGE,"E51"),sQuery(id+"F0.wireOp",EDGE,"E52"),sQuery(id+"F0.wireOp",EDGE,"E53")])],"isStart":true});
            var Q45;
            Q45=makeQuery(id+"F1.opExtrude","CAP_FACE",FACE,{"disambiguationData":[OSD([sQuery(id+"F0.wireOp",EDGE,"E4"),sQuery(id+"F0.wireOp",EDGE,"E6"),sQuery(id+"F0.wireOp",EDGE,"E7"),sQuery(id+"F0.wireOp",EDGE,"E8")])],"isStart":true});
            var Q46;
            Q46=makeQuery(id+"F1.opExtrude","CAP_FACE",FACE,{"disambiguationData":[OSD([sQuery(id+"F0.wireOp",EDGE,"E12"),sQuery(id+"F0.wireOp",EDGE,"E13"),sQuery(id+"F0.wireOp",EDGE,"E14")])],"isStart":true});
            var Q47;
            Q47=makeQuery(id+"F1.opExtrude","CAP_FACE",FACE,{"disambiguationData":[OSD([sQuery(id+"F0.wireOp",EDGE,"E15"),sQuery(id+"F0.wireOp",EDGE,"E18"),sQuery(id+"F0.wireOp",EDGE,"E19")])],"isStart":true});
            var Q48;
            Q48=makeQuery(id+"F1.opExtrude","CAP_FACE",FACE,{"disambiguationData":[OSD([sQuery(id+"F0.wireOp",EDGE,"E20"),sQuery(id+"F0.wireOp",EDGE,"E24"),sQuery(id+"F0.wireOp",EDGE,"E25")])],"isStart":true});
            var Q49;
            Q49=makeQuery(id+"F1.opExtrude","CAP_FACE",FACE,{"disambiguationData":[OSD([sQuery(id+"F0.wireOp",EDGE,"E26"),sQuery(id+"F0.wireOp",EDGE,"E27"),sQuery(id+"F0.wireOp",EDGE,"E28")])],"isStart":true});
            var Q50;
            Q50=makeQuery(id+"F1.opExtrude","CAP_FACE",FACE,{"disambiguationData":[OSD([sQuery(id+"F0.wireOp",EDGE,"E29"),sQuery(id+"F0.wireOp",EDGE,"E30"),sQuery(id+"F0.wireOp",EDGE,"E31")])],"isStart":true});
            var Q51;
            Q51=makeQuery(id+"F1.opExtrude","CAP_FACE",FACE,{"disambiguationData":[OSD([sQuery(id+"F0.wireOp",EDGE,"E32.MirrorCS"),sQuery(id+"F0.wireOp",EDGE,"E35.MirrorCS"),sQuery(id+"F0.wireOp",EDGE,"E38.MirrorCS")])],"isStart":true});
            var Q52;
            Q52=makeQuery(id+"F1.opExtrude","CAP_FACE",FACE,{"disambiguationData":[OSD([sQuery(id+"F0.wireOp",EDGE,"E36.MirrorCS"),sQuery(id+"F0.wireOp",EDGE,"E37.MirrorCS"),sQuery(id+"F0.wireOp",EDGE,"E39.MirrorCS")])],"isStart":true});
            var Q53;
            Q53=makeQuery(id+"F1.opExtrude","CAP_FACE",FACE,{"disambiguationData":[OSD([sQuery(id+"F0.wireOp",EDGE,"E33.MirrorCS"),sQuery(id+"F0.wireOp",EDGE,"E34.MirrorCS"),sQuery(id+"F0.wireOp",EDGE,"E85")])],"isStart":true});
            var Q54;
            Q54=makeQuery(id+"F1.opExtrude","CAP_FACE",FACE,{"disambiguationData":[OSD([sQuery(id+"F0.wireOp",EDGE,"E86"),sQuery(id+"F0.wireOp",EDGE,"E87"),sQuery(id+"F0.wireOp",EDGE,"E88")])],"isStart":true});
            var Q55;
            Q55=makeQuery(id+"F1.opExtrude","CAP_FACE",FACE,{"disambiguationData":[OSD([sQuery(id+"F0.wireOp",EDGE,"E86"),sQuery(id+"F0.wireOp",EDGE,"E93"),sQuery(id+"F0.wireOp",EDGE,"E94")])],"isStart":true});
            var Q56;
            Q56=makeQuery(id+"F1.opExtrude","CAP_FACE",FACE,{"disambiguationData":[OSD([sQuery(id+"F0.wireOp",EDGE,"E86"),sQuery(id+"F0.wireOp",EDGE,"E95"),sQuery(id+"F0.wireOp",EDGE,"E96")])],"isStart":true});
            var Q57;
            Q57=makeQuery(id+"F1.opExtrude","CAP_FACE",FACE,{"disambiguationData":[OSD([sQuery(id+"F0.wireOp",EDGE,"E86"),sQuery(id+"F0.wireOp",EDGE,"E97"),sQuery(id+"F0.wireOp",EDGE,"E98")])],"isStart":true});
            var Q58;
            Q58=makeQuery(id+"F1.opExtrude","CAP_FACE",FACE,{"disambiguationData":[OSD([sQuery(id+"F0.wireOp",EDGE,"E86"),sQuery(id+"F0.wireOp",EDGE,"E99"),sQuery(id+"F0.wireOp",EDGE,"E100")])],"isStart":true});
            var Q59;
            Q59=makeQuery(id+"F1.opExtrude","CAP_FACE",FACE,{"disambiguationData":[OSD([sQuery(id+"F0.wireOp",EDGE,"E86"),sQuery(id+"F0.wireOp",EDGE,"E101"),sQuery(id+"F0.wireOp",EDGE,"E102")])],"isStart":true});
            var Q60;
            Q60=makeQuery(id+"F1.opExtrude","CAP_FACE",FACE,{"disambiguationData":[OSD([sQuery(id+"F0.wireOp",EDGE,"E86"),sQuery(id+"F0.wireOp",EDGE,"E104"),sQuery(id+"F0.wireOp",EDGE,"E105")])],"isStart":true});
            var Q61;
            Q61=makeQuery(id+"F1.opExtrude","CAP_FACE",FACE,{"disambiguationData":[OSD([sQuery(id+"F0.wireOp",EDGE,"E40"),sQuery(id+"F0.wireOp",EDGE,"E84"),sQuery(id+"F0.wireOp",EDGE,"E103")])],"isStart":true});
            var Q62;
            Q62=makeQuery(id+"F1.opExtrude","CAP_FACE",FACE,{"disambiguationData":[OSD([sQuery(id+"F0.wireOp",EDGE,"E40"),sQuery(id+"F0.wireOp",EDGE,"E82"),sQuery(id+"F0.wireOp",EDGE,"E83")])],"isStart":true});
            var Q63;
            Q63=makeQuery(id+"F1.opExtrude","CAP_FACE",FACE,{"disambiguationData":[OSD([sQuery(id+"F0.wireOp",EDGE,"E40"),sQuery(id+"F0.wireOp",EDGE,"E80"),sQuery(id+"F0.wireOp",EDGE,"E81")])],"isStart":true});
            var Q64;
            Q64=makeQuery(id+"F1.opExtrude","CAP_FACE",FACE,{"disambiguationData":[OSD([sQuery(id+"F0.wireOp",EDGE,"E40"),sQuery(id+"F0.wireOp",EDGE,"E78"),sQuery(id+"F0.wireOp",EDGE,"E79")])],"isStart":true});
            var Q65;
            Q65=makeQuery(id+"F1.opExtrude","CAP_FACE",FACE,{"disambiguationData":[OSD([sQuery(id+"F0.wireOp",EDGE,"E40"),sQuery(id+"F0.wireOp",EDGE,"E76"),sQuery(id+"F0.wireOp",EDGE,"E77")])],"isStart":true});
            var Q66;
            Q66=makeQuery(id+"F1.opExtrude","CAP_FACE",FACE,{"disambiguationData":[OSD([sQuery(id+"F0.wireOp",EDGE,"E40"),sQuery(id+"F0.wireOp",EDGE,"E74"),sQuery(id+"F0.wireOp",EDGE,"E75")])],"isStart":true});
            var Q67;
            Q67=makeQuery(id+"F1.opExtrude","CAP_FACE",FACE,{"disambiguationData":[OSD([sQuery(id+"F0.wireOp",EDGE,"E40"),sQuery(id+"F0.wireOp",EDGE,"E72"),sQuery(id+"F0.wireOp",EDGE,"E73")])],"isStart":true});
            var Q68;
            Q68=makeQuery(id+"F1.opExtrude","CAP_FACE",FACE,{"disambiguationData":[OSD([sQuery(id+"F0.wireOp",EDGE,"E40"),sQuery(id+"F0.wireOp",EDGE,"E70"),sQuery(id+"F0.wireOp",EDGE,"E71")])],"isStart":true});
            var Q69;
            Q69=makeQuery(id+"F1.opExtrude","CAP_FACE",FACE,{"disambiguationData":[OSD([sQuery(id+"F0.wireOp",EDGE,"E40"),sQuery(id+"F0.wireOp",EDGE,"E68"),sQuery(id+"F0.wireOp",EDGE,"E69")])],"isStart":true});
            var Q70;
            Q70=makeQuery(id+"F1.opExtrude","CAP_FACE",FACE,{"disambiguationData":[OSD([sQuery(id+"F0.wireOp",EDGE,"E40"),sQuery(id+"F0.wireOp",EDGE,"E66"),sQuery(id+"F0.wireOp",EDGE,"E67")])],"isStart":true});
            var Q71;
            Q71=makeQuery(id+"F1.opExtrude","CAP_FACE",FACE,{"disambiguationData":[OSD([sQuery(id+"F0.wireOp",EDGE,"E40"),sQuery(id+"F0.wireOp",EDGE,"E64"),sQuery(id+"F0.wireOp",EDGE,"E65")])],"isStart":true});
            var Q72;
            Q72=makeQuery(id+"F1.opExtrude","CAP_FACE",FACE,{"disambiguationData":[OSD([sQuery(id+"F0.wireOp",EDGE,"E40"),sQuery(id+"F0.wireOp",EDGE,"E48"),sQuery(id+"F0.wireOp",EDGE,"E56")])],"isStart":true});
            var Q73;
            Q73=makeQuery(id+"F1.opExtrude","CAP_FACE",FACE,{"disambiguationData":[OSD([sQuery(id+"F0.wireOp",EDGE,"E40"),sQuery(id+"F0.wireOp",EDGE,"E44"),sQuery(id+"F0.wireOp",EDGE,"E47")])],"isStart":true});
            var Q74;
            Q74=makeQuery(id+"F1.opExtrude","CAP_FACE",FACE,{"disambiguationData":[OSD([sQuery(id+"F0.wireOp",EDGE,"E1"),sQuery(id+"F0.wireOp",EDGE,"E40"),sQuery(id+"F0.wireOp",EDGE,"E43")])],"isStart":true});
            var Q75;
            Q75=makeQuery(id+"F1.opExtrude","CAP_FACE",FACE,{"disambiguationData":[OSD([sQuery(id+"F0.wireOp",EDGE,"E2"),sQuery(id+"F0.wireOp",EDGE,"E9"),sQuery(id+"F0.wireOp",EDGE,"E10")])],"isStart":true});
            shell(context, id + "F2", {"entities" : qUnion([Q0, Q1, Q2, Q3, Q4, Q5, Q6, Q7, Q8, Q9, Q10, Q11, Q12, Q13, Q14, Q15, Q16, Q17, Q18, Q19, Q20, Q21, Q22, Q23, Q24, Q25, Q26, Q27, Q28, Q29, Q30, Q31, Q32, Q33, Q34, Q35, Q36, Q37, Q38, Q39, Q40, Q41, Q42, Q43, Q44, Q45, Q46, Q47, Q48, Q49, Q50, Q51, Q52, Q53, Q54, Q55, Q56, Q57, Q58, Q59, Q60, Q61, Q62, Q63, Q64, Q65, Q66, Q67, Q68, Q69, Q70, Q71, Q72, Q73, Q74, Q75]), "thickness" : 20 * mm});
        }
        {
            var Q0;
            {var subQ0=sQuery(id+"F0.wireOp",EDGE,"E105");Q0=makeQuery(id+"F0.imprint","IMPRINT",FACE,{"disambiguationData":[TD([[makeQuery(id+"F0.imprint","IMPRINT",EDGE,{"derivedFrom":subQ0}),-1.0]])]});}
            var Q1;
            {var subQ0=sQuery(id+"F0.wireOp",EDGE,"E103");Q1=makeQuery(id+"F0.imprint","IMPRINT",FACE,{"disambiguationData":[TD([[makeQuery(id+"F0.imprint","IMPRINT",EDGE,{"derivedFrom":subQ0}),1.0]])]});}
            var Q2;
            Q2=makeQuery(id+"F0.imprint","IMPRINT",FACE,{"disambiguationData":[TD([[makeQuery(id+"F0.imprint","IMPRINT",EDGE,{"derivedFrom":sQuery(id+"F0.wireOp",EDGE,"E100")}),-1.0]])]});
            var Q3;
            Q3=makeQuery(id+"F0.imprint","IMPRINT",FACE,{"disambiguationData":[TD([[makeQuery(id+"F0.imprint","IMPRINT",EDGE,{"derivedFrom":sQuery(id+"F0.wireOp",EDGE,"E81")}),1.0]])]});
            var Q4;
            Q4=makeQuery(id+"F0.imprint","IMPRINT",FACE,{"disambiguationData":[TD([[makeQuery(id+"F0.imprint","IMPRINT",EDGE,{"derivedFrom":sQuery(id+"F0.wireOp",EDGE,"E96")}),-1.0]])]});
            var Q5;
            Q5=makeQuery(id+"F0.imprint","IMPRINT",FACE,{"disambiguationData":[TD([[makeQuery(id+"F0.imprint","IMPRINT",EDGE,{"derivedFrom":sQuery(id+"F0.wireOp",EDGE,"E77")}),1.0]])]});
            var Q6;
            Q6=makeQuery(id+"F0.imprint","IMPRINT",FACE,{"disambiguationData":[TD([[makeQuery(id+"F0.imprint","IMPRINT",EDGE,{"derivedFrom":sQuery(id+"F0.wireOp",EDGE,"E73")}),1.0]])]});
            var Q7;
            Q7=makeQuery(id+"F0.imprint","IMPRINT",FACE,{"disambiguationData":[TD([[makeQuery(id+"F0.imprint","IMPRINT",EDGE,{"derivedFrom":sQuery(id+"F0.wireOp",EDGE,"E88")}),-1.0]])]});
            var Q8;
            Q8=makeQuery(id+"F0.imprint","IMPRINT",FACE,{"disambiguationData":[TD([[makeQuery(id+"F0.imprint","IMPRINT",EDGE,{"derivedFrom":sQuery(id+"F0.wireOp",EDGE,"E33.MirrorCS")}),1.0]])]});
            var Q9;
            Q9=makeQuery(id+"F0.imprint","IMPRINT",FACE,{"disambiguationData":[TD([[makeQuery(id+"F0.imprint","IMPRINT",EDGE,{"derivedFrom":sQuery(id+"F0.wireOp",EDGE,"E69")}),1.0]])]});
            var Q10;
            Q10=makeQuery(id+"F0.imprint","IMPRINT",FACE,{"disambiguationData":[TD([[makeQuery(id+"F0.imprint","IMPRINT",EDGE,{"derivedFrom":sQuery(id+"F0.wireOp",EDGE,"E63")}),1.0]])]});
            var Q11;
            Q11=makeQuery(id+"F0.imprint","IMPRINT",FACE,{"disambiguationData":[TD([[makeQuery(id+"F0.imprint","IMPRINT",EDGE,{"derivedFrom":sQuery(id+"F0.wireOp",EDGE,"E30")}),-1.0]])]});
            var Q12;
            Q12=makeQuery(id+"F0.imprint","IMPRINT",FACE,{"disambiguationData":[TD([[makeQuery(id+"F0.imprint","IMPRINT",EDGE,{"derivedFrom":sQuery(id+"F0.wireOp",EDGE,"E21")}),1.0]])]});
            var Q13;
            Q13=makeQuery(id+"F0.imprint","IMPRINT",FACE,{"disambiguationData":[TD([[makeQuery(id+"F0.imprint","IMPRINT",EDGE,{"derivedFrom":sQuery(id+"F0.wireOp",EDGE,"E45")}),-1.0]])]});
            var Q14;
            Q14=makeQuery(id+"F0.imprint","IMPRINT",FACE,{"disambiguationData":[TD([[makeQuery(id+"F0.imprint","IMPRINT",EDGE,{"derivedFrom":sQuery(id+"F0.wireOp",EDGE,"E7")}),-1.0]])]});
            var Q15;
            Q15=makeQuery(id+"F0.imprint","IMPRINT",FACE,{"disambiguationData":[TD([[makeQuery(id+"F0.imprint","IMPRINT",EDGE,{"derivedFrom":sQuery(id+"F0.wireOp",EDGE,"E0")}),-1.0]])]});
            extrude(context, id + "F3", {"entities" : qUnion([Q0, Q1, Q2, Q3, Q4, Q5, Q6, Q7, Q8, Q9, Q10, Q11, Q12, Q13, Q14, Q15]), "depth" : 100 * mm, "offsetDistance" : 25 * mm});
        }
        {
            var Q0;
            Q0=makeQuery(id+"F3.opExtrude","CAP_FACE",FACE,{"disambiguationData":[OSD([sQuery(id+"F0.wireOp",EDGE,"E105"),sQuery(id+"F0.wireOp",EDGE,"E106"),sQuery(id+"F0.wireOp",EDGE,"E169"),sQuery(id+"F0.wireOp",EDGE,"E174")])],"isStart":false});
            var Q1;
            Q1=makeQuery(id+"F3.opExtrude","CAP_FACE",FACE,{"disambiguationData":[OSD([sQuery(id+"F0.wireOp",EDGE,"E103"),sQuery(id+"F0.wireOp",EDGE,"E106"),sQuery(id+"F0.wireOp",EDGE,"E172"),sQuery(id+"F0.wireOp",EDGE,"E173")])],"isStart":false});
            var Q2;
            Q2=makeQuery(id+"F3.opExtrude","CAP_FACE",FACE,{"disambiguationData":[OSD([sQuery(id+"F0.wireOp",EDGE,"E81"),sQuery(id+"F0.wireOp",EDGE,"E82"),sQuery(id+"F0.wireOp",EDGE,"E154"),sQuery(id+"F0.wireOp",EDGE,"E162"),sQuery(id+"F0.wireOp",EDGE,"E164"),sQuery(id+"F0.wireOp",EDGE,"E165")])],"isStart":false});
            var Q3;
            Q3=makeQuery(id+"F3.opExtrude","CAP_FACE",FACE,{"disambiguationData":[OSD([sQuery(id+"F0.wireOp",EDGE,"E100"),sQuery(id+"F0.wireOp",EDGE,"E101"),sQuery(id+"F0.wireOp",EDGE,"E157"),sQuery(id+"F0.wireOp",EDGE,"E159"),sQuery(id+"F0.wireOp",EDGE,"E160"),sQuery(id+"F0.wireOp",EDGE,"E161")])],"isStart":false});
            var Q4;
            Q4=makeQuery(id+"F3.opExtrude","CAP_FACE",FACE,{"disambiguationData":[OSD([sQuery(id+"F0.wireOp",EDGE,"E96"),sQuery(id+"F0.wireOp",EDGE,"E97"),sQuery(id+"F0.wireOp",EDGE,"E144"),sQuery(id+"F0.wireOp",EDGE,"E145"),sQuery(id+"F0.wireOp",EDGE,"E146"),sQuery(id+"F0.wireOp",EDGE,"E151")])],"isStart":false});
            var Q5;
            Q5=makeQuery(id+"F3.opExtrude","CAP_FACE",FACE,{"disambiguationData":[OSD([sQuery(id+"F0.wireOp",EDGE,"E77"),sQuery(id+"F0.wireOp",EDGE,"E78"),sQuery(id+"F0.wireOp",EDGE,"E141"),sQuery(id+"F0.wireOp",EDGE,"E148"),sQuery(id+"F0.wireOp",EDGE,"E149"),sQuery(id+"F0.wireOp",EDGE,"E150")])],"isStart":false});
            var Q6;
            Q6=makeQuery(id+"F3.opExtrude","CAP_FACE",FACE,{"disambiguationData":[OSD([sQuery(id+"F0.wireOp",EDGE,"E73"),sQuery(id+"F0.wireOp",EDGE,"E74"),sQuery(id+"F0.wireOp",EDGE,"E130"),sQuery(id+"F0.wireOp",EDGE,"E131"),sQuery(id+"F0.wireOp",EDGE,"E132"),sQuery(id+"F0.wireOp",EDGE,"E133")])],"isStart":false});
            var Q7;
            Q7=makeQuery(id+"F3.opExtrude","CAP_FACE",FACE,{"disambiguationData":[OSD([sQuery(id+"F0.wireOp",EDGE,"E88"),sQuery(id+"F0.wireOp",EDGE,"E89"),sQuery(id+"F0.wireOp",EDGE,"E93"),sQuery(id+"F0.wireOp",EDGE,"E134"),sQuery(id+"F0.wireOp",EDGE,"E136"),sQuery(id+"F0.wireOp",EDGE,"E137")])],"isStart":false});
            var Q8;
            Q8=makeQuery(id+"F3.opExtrude","CAP_FACE",FACE,{"disambiguationData":[OSD([sQuery(id+"F0.wireOp",EDGE,"E33.MirrorCS"),sQuery(id+"F0.wireOp",EDGE,"E37.MirrorCS"),sQuery(id+"F0.wireOp",EDGE,"E92"),sQuery(id+"F0.wireOp",EDGE,"E114"),sQuery(id+"F0.wireOp",EDGE,"E121"),sQuery(id+"F0.wireOp",EDGE,"E122")])],"isStart":false});
            var Q9;
            Q9=makeQuery(id+"F3.opExtrude","CAP_FACE",FACE,{"disambiguationData":[OSD([sQuery(id+"F0.wireOp",EDGE,"E69"),sQuery(id+"F0.wireOp",EDGE,"E70"),sQuery(id+"F0.wireOp",EDGE,"E120"),sQuery(id+"F0.wireOp",EDGE,"E125"),sQuery(id+"F0.wireOp",EDGE,"E127"),sQuery(id+"F0.wireOp",EDGE,"E128")])],"isStart":false});
            var Q10;
            Q10=makeQuery(id+"F3.opExtrude","CAP_FACE",FACE,{"disambiguationData":[OSD([sQuery(id+"F0.wireOp",EDGE,"E63"),sQuery(id+"F0.wireOp",EDGE,"E65"),sQuery(id+"F0.wireOp",EDGE,"E66"),sQuery(id+"F0.wireOp",EDGE,"E107"),sQuery(id+"F0.wireOp",EDGE,"E108"),sQuery(id+"F0.wireOp",EDGE,"E109")])],"isStart":false});
            var Q11;
            Q11=makeQuery(id+"F3.opExtrude","CAP_FACE",FACE,{"disambiguationData":[OSD([sQuery(id+"F0.wireOp",EDGE,"E30"),sQuery(id+"F0.wireOp",EDGE,"E38.MirrorCS"),sQuery(id+"F0.wireOp",EDGE,"E60"),sQuery(id+"F0.wireOp",EDGE,"E111"),sQuery(id+"F0.wireOp",EDGE,"E112"),sQuery(id+"F0.wireOp",EDGE,"E113")])],"isStart":false});
            var Q12;
            Q12=makeQuery(id+"F3.opExtrude","CAP_FACE",FACE,{"disambiguationData":[OSD([sQuery(id+"F0.wireOp",EDGE,"E21"),sQuery(id+"F0.wireOp",EDGE,"E24"),sQuery(id+"F0.wireOp",EDGE,"E26"),sQuery(id+"F0.wireOp",EDGE,"E52"),sQuery(id+"F0.wireOp",EDGE,"E54"),sQuery(id+"F0.wireOp",EDGE,"E55")])],"isStart":false});
            var Q13;
            Q13=makeQuery(id+"F3.opExtrude","CAP_FACE",FACE,{"disambiguationData":[OSD([sQuery(id+"F0.wireOp",EDGE,"E45"),sQuery(id+"F0.wireOp",EDGE,"E47"),sQuery(id+"F0.wireOp",EDGE,"E48"),sQuery(id+"F0.wireOp",EDGE,"E49"),sQuery(id+"F0.wireOp",EDGE,"E50"),sQuery(id+"F0.wireOp",EDGE,"E53")])],"isStart":false});
            var Q14;
            Q14=makeQuery(id+"F3.opExtrude","CAP_FACE",FACE,{"disambiguationData":[OSD([sQuery(id+"F0.wireOp",EDGE,"E0"),sQuery(id+"F0.wireOp",EDGE,"E1"),sQuery(id+"F0.wireOp",EDGE,"E2"),sQuery(id+"F0.wireOp",EDGE,"E3"),sQuery(id+"F0.wireOp",EDGE,"E4"),sQuery(id+"F0.wireOp",EDGE,"E5")])],"isStart":false});
            var Q15;
            Q15=makeQuery(id+"F3.opExtrude","CAP_FACE",FACE,{"disambiguationData":[OSD([sQuery(id+"F0.wireOp",EDGE,"E7"),sQuery(id+"F0.wireOp",EDGE,"E11"),sQuery(id+"F0.wireOp",EDGE,"E12"),sQuery(id+"F0.wireOp",EDGE,"E15"),sQuery(id+"F0.wireOp",EDGE,"E16"),sQuery(id+"F0.wireOp",EDGE,"E17")])],"isStart":false});
            var Q16;
            Q16=makeQuery(id+"F3.opExtrude","CAP_FACE",FACE,{"disambiguationData":[OSD([sQuery(id+"F0.wireOp",EDGE,"E103"),sQuery(id+"F0.wireOp",EDGE,"E106"),sQuery(id+"F0.wireOp",EDGE,"E172"),sQuery(id+"F0.wireOp",EDGE,"E173")])],"isStart":true});
            var Q17;
            Q17=makeQuery(id+"F3.opExtrude","CAP_FACE",FACE,{"disambiguationData":[OSD([sQuery(id+"F0.wireOp",EDGE,"E105"),sQuery(id+"F0.wireOp",EDGE,"E106"),sQuery(id+"F0.wireOp",EDGE,"E169"),sQuery(id+"F0.wireOp",EDGE,"E174")])],"isStart":true});
            var Q18;
            Q18=makeQuery(id+"F3.opExtrude","CAP_FACE",FACE,{"disambiguationData":[OSD([sQuery(id+"F0.wireOp",EDGE,"E100"),sQuery(id+"F0.wireOp",EDGE,"E101"),sQuery(id+"F0.wireOp",EDGE,"E157"),sQuery(id+"F0.wireOp",EDGE,"E159"),sQuery(id+"F0.wireOp",EDGE,"E160"),sQuery(id+"F0.wireOp",EDGE,"E161")])],"isStart":true});
            var Q19;
            Q19=makeQuery(id+"F3.opExtrude","CAP_FACE",FACE,{"disambiguationData":[OSD([sQuery(id+"F0.wireOp",EDGE,"E81"),sQuery(id+"F0.wireOp",EDGE,"E82"),sQuery(id+"F0.wireOp",EDGE,"E154"),sQuery(id+"F0.wireOp",EDGE,"E162"),sQuery(id+"F0.wireOp",EDGE,"E164"),sQuery(id+"F0.wireOp",EDGE,"E165")])],"isStart":true});
            var Q20;
            Q20=makeQuery(id+"F3.opExtrude","CAP_FACE",FACE,{"disambiguationData":[OSD([sQuery(id+"F0.wireOp",EDGE,"E77"),sQuery(id+"F0.wireOp",EDGE,"E78"),sQuery(id+"F0.wireOp",EDGE,"E141"),sQuery(id+"F0.wireOp",EDGE,"E148"),sQuery(id+"F0.wireOp",EDGE,"E149"),sQuery(id+"F0.wireOp",EDGE,"E150")])],"isStart":true});
            var Q21;
            Q21=makeQuery(id+"F3.opExtrude","CAP_FACE",FACE,{"disambiguationData":[OSD([sQuery(id+"F0.wireOp",EDGE,"E96"),sQuery(id+"F0.wireOp",EDGE,"E97"),sQuery(id+"F0.wireOp",EDGE,"E144"),sQuery(id+"F0.wireOp",EDGE,"E145"),sQuery(id+"F0.wireOp",EDGE,"E146"),sQuery(id+"F0.wireOp",EDGE,"E151")])],"isStart":true});
            var Q22;
            Q22=makeQuery(id+"F3.opExtrude","CAP_FACE",FACE,{"disambiguationData":[OSD([sQuery(id+"F0.wireOp",EDGE,"E88"),sQuery(id+"F0.wireOp",EDGE,"E89"),sQuery(id+"F0.wireOp",EDGE,"E93"),sQuery(id+"F0.wireOp",EDGE,"E134"),sQuery(id+"F0.wireOp",EDGE,"E136"),sQuery(id+"F0.wireOp",EDGE,"E137")])],"isStart":true});
            var Q23;
            Q23=makeQuery(id+"F3.opExtrude","CAP_FACE",FACE,{"disambiguationData":[OSD([sQuery(id+"F0.wireOp",EDGE,"E73"),sQuery(id+"F0.wireOp",EDGE,"E74"),sQuery(id+"F0.wireOp",EDGE,"E130"),sQuery(id+"F0.wireOp",EDGE,"E131"),sQuery(id+"F0.wireOp",EDGE,"E132"),sQuery(id+"F0.wireOp",EDGE,"E133")])],"isStart":true});
            var Q24;
            Q24=makeQuery(id+"F3.opExtrude","CAP_FACE",FACE,{"disambiguationData":[OSD([sQuery(id+"F0.wireOp",EDGE,"E69"),sQuery(id+"F0.wireOp",EDGE,"E70"),sQuery(id+"F0.wireOp",EDGE,"E120"),sQuery(id+"F0.wireOp",EDGE,"E125"),sQuery(id+"F0.wireOp",EDGE,"E127"),sQuery(id+"F0.wireOp",EDGE,"E128")])],"isStart":true});
            var Q25;
            Q25=makeQuery(id+"F3.opExtrude","CAP_FACE",FACE,{"disambiguationData":[OSD([sQuery(id+"F0.wireOp",EDGE,"E33.MirrorCS"),sQuery(id+"F0.wireOp",EDGE,"E37.MirrorCS"),sQuery(id+"F0.wireOp",EDGE,"E92"),sQuery(id+"F0.wireOp",EDGE,"E114"),sQuery(id+"F0.wireOp",EDGE,"E121"),sQuery(id+"F0.wireOp",EDGE,"E122")])],"isStart":true});
            var Q26;
            Q26=makeQuery(id+"F3.opExtrude","CAP_FACE",FACE,{"disambiguationData":[OSD([sQuery(id+"F0.wireOp",EDGE,"E30"),sQuery(id+"F0.wireOp",EDGE,"E38.MirrorCS"),sQuery(id+"F0.wireOp",EDGE,"E60"),sQuery(id+"F0.wireOp",EDGE,"E111"),sQuery(id+"F0.wireOp",EDGE,"E112"),sQuery(id+"F0.wireOp",EDGE,"E113")])],"isStart":true});
            var Q27;
            Q27=makeQuery(id+"F3.opExtrude","CAP_FACE",FACE,{"disambiguationData":[OSD([sQuery(id+"F0.wireOp",EDGE,"E63"),sQuery(id+"F0.wireOp",EDGE,"E65"),sQuery(id+"F0.wireOp",EDGE,"E66"),sQuery(id+"F0.wireOp",EDGE,"E107"),sQuery(id+"F0.wireOp",EDGE,"E108"),sQuery(id+"F0.wireOp",EDGE,"E109")])],"isStart":true});
            var Q28;
            Q28=makeQuery(id+"F3.opExtrude","CAP_FACE",FACE,{"disambiguationData":[OSD([sQuery(id+"F0.wireOp",EDGE,"E45"),sQuery(id+"F0.wireOp",EDGE,"E47"),sQuery(id+"F0.wireOp",EDGE,"E48"),sQuery(id+"F0.wireOp",EDGE,"E49"),sQuery(id+"F0.wireOp",EDGE,"E50"),sQuery(id+"F0.wireOp",EDGE,"E53")])],"isStart":true});
            var Q29;
            Q29=makeQuery(id+"F3.opExtrude","CAP_FACE",FACE,{"disambiguationData":[OSD([sQuery(id+"F0.wireOp",EDGE,"E21"),sQuery(id+"F0.wireOp",EDGE,"E24"),sQuery(id+"F0.wireOp",EDGE,"E26"),sQuery(id+"F0.wireOp",EDGE,"E52"),sQuery(id+"F0.wireOp",EDGE,"E54"),sQuery(id+"F0.wireOp",EDGE,"E55")])],"isStart":true});
            var Q30;
            Q30=makeQuery(id+"F3.opExtrude","CAP_FACE",FACE,{"disambiguationData":[OSD([sQuery(id+"F0.wireOp",EDGE,"E7"),sQuery(id+"F0.wireOp",EDGE,"E11"),sQuery(id+"F0.wireOp",EDGE,"E12"),sQuery(id+"F0.wireOp",EDGE,"E15"),sQuery(id+"F0.wireOp",EDGE,"E16"),sQuery(id+"F0.wireOp",EDGE,"E17")])],"isStart":true});
            var Q31;
            Q31=makeQuery(id+"F3.opExtrude","CAP_FACE",FACE,{"disambiguationData":[OSD([sQuery(id+"F0.wireOp",EDGE,"E0"),sQuery(id+"F0.wireOp",EDGE,"E1"),sQuery(id+"F0.wireOp",EDGE,"E2"),sQuery(id+"F0.wireOp",EDGE,"E3"),sQuery(id+"F0.wireOp",EDGE,"E4"),sQuery(id+"F0.wireOp",EDGE,"E5")])],"isStart":true});
            shell(context, id + "F4", {"entities" : qUnion([Q0, Q1, Q2, Q3, Q4, Q5, Q6, Q7, Q8, Q9, Q10, Q11, Q12, Q13, Q14, Q15, Q16, Q17, Q18, Q19, Q20, Q21, Q22, Q23, Q24, Q25, Q26, Q27, Q28, Q29, Q30, Q31]), "thickness" : 20 * mm});
        }
        {
            var Q0;
            Q0=makeQuery(id+"F0.imprint","IMPRINT",FACE,{"disambiguationData":[TD([[makeQuery(id+"F0.imprint","IMPRINT",EDGE,{"derivedFrom":sQuery(id+"F0.wireOp",EDGE,"E160")}),1.0]])]});
            var Q1;
            Q1=makeQuery(id+"F0.imprint","IMPRINT",FACE,{"disambiguationData":[TD([[makeQuery(id+"F0.imprint","IMPRINT",EDGE,{"derivedFrom":sQuery(id+"F0.wireOp",EDGE,"E146")}),1.0]])]});
            var Q2;
            Q2=makeQuery(id+"F0.imprint","IMPRINT",FACE,{"disambiguationData":[TD([[makeQuery(id+"F0.imprint","IMPRINT",EDGE,{"derivedFrom":sQuery(id+"F0.wireOp",EDGE,"E132")}),-1.0]])]});
            var Q3;
            Q3=makeQuery(id+"F0.imprint","IMPRINT",FACE,{"disambiguationData":[TD([[makeQuery(id+"F0.imprint","IMPRINT",EDGE,{"derivedFrom":sQuery(id+"F0.wireOp",EDGE,"E91")}),1.0]])]});
            var Q4;
            Q4=makeQuery(id+"F0.imprint","IMPRINT",FACE,{"disambiguationData":[TD([[makeQuery(id+"F0.imprint","IMPRINT",EDGE,{"derivedFrom":sQuery(id+"F0.wireOp",EDGE,"E108")}),1.0]])]});
            var Q5;
            Q5=makeQuery(id+"F0.imprint","IMPRINT",FACE,{"disambiguationData":[TD([[makeQuery(id+"F0.imprint","IMPRINT",EDGE,{"derivedFrom":sQuery(id+"F0.wireOp",EDGE,"E50")}),-1.0]])]});
            var Q6;
            Q6=makeQuery(id+"F0.imprint","IMPRINT",FACE,{"disambiguationData":[TD([[makeQuery(id+"F0.imprint","IMPRINT",EDGE,{"derivedFrom":sQuery(id+"F0.wireOp",EDGE,"E5")}),1.0]])]});
            extrude(context, id + "F5", {"entities" : qUnion([Q0, Q1, Q2, Q3, Q4, Q5, Q6]), "depth" : 100 * mm, "offsetDistance" : 25 * mm});
        }
        {
            var Q0;
            Q0=makeQuery(id+"F5.opExtrude","CAP_FACE",FACE,{"disambiguationData":[OSD([sQuery(id+"F0.wireOp",EDGE,"E160"),sQuery(id+"F0.wireOp",EDGE,"E163"),sQuery(id+"F0.wireOp",EDGE,"E164"),sQuery(id+"F0.wireOp",EDGE,"E166"),sQuery(id+"F0.wireOp",EDGE,"E167"),sQuery(id+"F0.wireOp",EDGE,"E168")])],"isStart":false});
            var Q1;
            Q1=makeQuery(id+"F5.opExtrude","CAP_FACE",FACE,{"disambiguationData":[OSD([sQuery(id+"F0.wireOp",EDGE,"E146"),sQuery(id+"F0.wireOp",EDGE,"E147"),sQuery(id+"F0.wireOp",EDGE,"E148"),sQuery(id+"F0.wireOp",EDGE,"E152"),sQuery(id+"F0.wireOp",EDGE,"E155"),sQuery(id+"F0.wireOp",EDGE,"E156")])],"isStart":false});
            var Q2;
            Q2=makeQuery(id+"F5.opExtrude","CAP_FACE",FACE,{"disambiguationData":[OSD([sQuery(id+"F0.wireOp",EDGE,"E132"),sQuery(id+"F0.wireOp",EDGE,"E135"),sQuery(id+"F0.wireOp",EDGE,"E137"),sQuery(id+"F0.wireOp",EDGE,"E138"),sQuery(id+"F0.wireOp",EDGE,"E139"),sQuery(id+"F0.wireOp",EDGE,"E140")])],"isStart":false});
            var Q3;
            Q3=makeQuery(id+"F5.opExtrude","CAP_FACE",FACE,{"disambiguationData":[OSD([sQuery(id+"F0.wireOp",EDGE,"E91"),sQuery(id+"F0.wireOp",EDGE,"E122"),sQuery(id+"F0.wireOp",EDGE,"E123"),sQuery(id+"F0.wireOp",EDGE,"E124"),sQuery(id+"F0.wireOp",EDGE,"E125"),sQuery(id+"F0.wireOp",EDGE,"E126")])],"isStart":false});
            var Q4;
            Q4=makeQuery(id+"F5.opExtrude","CAP_FACE",FACE,{"disambiguationData":[OSD([sQuery(id+"F0.wireOp",EDGE,"E108"),sQuery(id+"F0.wireOp",EDGE,"E110"),sQuery(id+"F0.wireOp",EDGE,"E113"),sQuery(id+"F0.wireOp",EDGE,"E116"),sQuery(id+"F0.wireOp",EDGE,"E117"),sQuery(id+"F0.wireOp",EDGE,"E118")])],"isStart":false});
            var Q5;
            Q5=makeQuery(id+"F5.opExtrude","CAP_FACE",FACE,{"disambiguationData":[OSD([sQuery(id+"F0.wireOp",EDGE,"E50"),sQuery(id+"F0.wireOp",EDGE,"E51"),sQuery(id+"F0.wireOp",EDGE,"E55"),sQuery(id+"F0.wireOp",EDGE,"E57"),sQuery(id+"F0.wireOp",EDGE,"E58"),sQuery(id+"F0.wireOp",EDGE,"E59")])],"isStart":false});
            var Q6;
            Q6=makeQuery(id+"F5.opExtrude","CAP_FACE",FACE,{"disambiguationData":[OSD([sQuery(id+"F0.wireOp",EDGE,"E5"),sQuery(id+"F0.wireOp",EDGE,"E6"),sQuery(id+"F0.wireOp",EDGE,"E17"),sQuery(id+"F0.wireOp",EDGE,"E23"),sQuery(id+"F0.wireOp",EDGE,"E41"),sQuery(id+"F0.wireOp",EDGE,"E42")])],"isStart":false});
            var Q7;
            Q7=makeQuery(id+"F5.opExtrude","CAP_FACE",FACE,{"disambiguationData":[OSD([sQuery(id+"F0.wireOp",EDGE,"E160"),sQuery(id+"F0.wireOp",EDGE,"E163"),sQuery(id+"F0.wireOp",EDGE,"E164"),sQuery(id+"F0.wireOp",EDGE,"E166"),sQuery(id+"F0.wireOp",EDGE,"E167"),sQuery(id+"F0.wireOp",EDGE,"E168")])],"isStart":true});
            var Q8;
            Q8=makeQuery(id+"F5.opExtrude","CAP_FACE",FACE,{"disambiguationData":[OSD([sQuery(id+"F0.wireOp",EDGE,"E146"),sQuery(id+"F0.wireOp",EDGE,"E147"),sQuery(id+"F0.wireOp",EDGE,"E148"),sQuery(id+"F0.wireOp",EDGE,"E152"),sQuery(id+"F0.wireOp",EDGE,"E155"),sQuery(id+"F0.wireOp",EDGE,"E156")])],"isStart":true});
            var Q9;
            Q9=makeQuery(id+"F5.opExtrude","CAP_FACE",FACE,{"disambiguationData":[OSD([sQuery(id+"F0.wireOp",EDGE,"E132"),sQuery(id+"F0.wireOp",EDGE,"E135"),sQuery(id+"F0.wireOp",EDGE,"E137"),sQuery(id+"F0.wireOp",EDGE,"E138"),sQuery(id+"F0.wireOp",EDGE,"E139"),sQuery(id+"F0.wireOp",EDGE,"E140")])],"isStart":true});
            var Q10;
            Q10=makeQuery(id+"F5.opExtrude","CAP_FACE",FACE,{"disambiguationData":[OSD([sQuery(id+"F0.wireOp",EDGE,"E91"),sQuery(id+"F0.wireOp",EDGE,"E122"),sQuery(id+"F0.wireOp",EDGE,"E123"),sQuery(id+"F0.wireOp",EDGE,"E124"),sQuery(id+"F0.wireOp",EDGE,"E125"),sQuery(id+"F0.wireOp",EDGE,"E126")])],"isStart":true});
            var Q11;
            Q11=makeQuery(id+"F5.opExtrude","CAP_FACE",FACE,{"disambiguationData":[OSD([sQuery(id+"F0.wireOp",EDGE,"E108"),sQuery(id+"F0.wireOp",EDGE,"E110"),sQuery(id+"F0.wireOp",EDGE,"E113"),sQuery(id+"F0.wireOp",EDGE,"E116"),sQuery(id+"F0.wireOp",EDGE,"E117"),sQuery(id+"F0.wireOp",EDGE,"E118")])],"isStart":true});
            var Q12;
            Q12=makeQuery(id+"F5.opExtrude","CAP_FACE",FACE,{"disambiguationData":[OSD([sQuery(id+"F0.wireOp",EDGE,"E50"),sQuery(id+"F0.wireOp",EDGE,"E51"),sQuery(id+"F0.wireOp",EDGE,"E55"),sQuery(id+"F0.wireOp",EDGE,"E57"),sQuery(id+"F0.wireOp",EDGE,"E58"),sQuery(id+"F0.wireOp",EDGE,"E59")])],"isStart":true});
            var Q13;
            Q13=makeQuery(id+"F5.opExtrude","CAP_FACE",FACE,{"disambiguationData":[OSD([sQuery(id+"F0.wireOp",EDGE,"E5"),sQuery(id+"F0.wireOp",EDGE,"E6"),sQuery(id+"F0.wireOp",EDGE,"E17"),sQuery(id+"F0.wireOp",EDGE,"E23"),sQuery(id+"F0.wireOp",EDGE,"E41"),sQuery(id+"F0.wireOp",EDGE,"E42")])],"isStart":true});
            shell(context, id + "F6", {"entities" : qUnion([Q0, Q1, Q2, Q3, Q4, Q5, Q6, Q7, Q8, Q9, Q10, Q11, Q12, Q13]), "thickness" : 20 * mm});
        }
        {
            var Q0;
            Q0=makeQuery(id+"F0.imprint","IMPRINT",FACE,{"disambiguationData":[TD([[makeQuery(id+"F0.imprint","IMPRINT",EDGE,{"derivedFrom":sQuery(id+"F0.wireOp",EDGE,"E102")}),-1.0]])]});
            var Q1;
            Q1=makeQuery(id+"F0.imprint","IMPRINT",FACE,{"disambiguationData":[TD([[makeQuery(id+"F0.imprint","IMPRINT",EDGE,{"derivedFrom":sQuery(id+"F0.wireOp",EDGE,"E83")}),1.0]])]});
            var Q2;
            Q2=makeQuery(id+"F0.imprint","IMPRINT",FACE,{"disambiguationData":[TD([[makeQuery(id+"F0.imprint","IMPRINT",EDGE,{"derivedFrom":sQuery(id+"F0.wireOp",EDGE,"E79")}),1.0]])]});
            var Q3;
            Q3=makeQuery(id+"F0.imprint","IMPRINT",FACE,{"disambiguationData":[TD([[makeQuery(id+"F0.imprint","IMPRINT",EDGE,{"derivedFrom":sQuery(id+"F0.wireOp",EDGE,"E98")}),-1.0]])]});
            var Q4;
            Q4=makeQuery(id+"F0.imprint","IMPRINT",FACE,{"disambiguationData":[TD([[makeQuery(id+"F0.imprint","IMPRINT",EDGE,{"derivedFrom":sQuery(id+"F0.wireOp",EDGE,"E94")}),-1.0]])]});
            var Q5;
            Q5=makeQuery(id+"F0.imprint","IMPRINT",FACE,{"disambiguationData":[TD([[makeQuery(id+"F0.imprint","IMPRINT",EDGE,{"derivedFrom":sQuery(id+"F0.wireOp",EDGE,"E75")}),1.0]])]});
            var Q6;
            Q6=makeQuery(id+"F0.imprint","IMPRINT",FACE,{"disambiguationData":[TD([[makeQuery(id+"F0.imprint","IMPRINT",EDGE,{"derivedFrom":sQuery(id+"F0.wireOp",EDGE,"E71")}),1.0]])]});
            var Q7;
            Q7=makeQuery(id+"F0.imprint","IMPRINT",FACE,{"disambiguationData":[TD([[makeQuery(id+"F0.imprint","IMPRINT",EDGE,{"derivedFrom":sQuery(id+"F0.wireOp",EDGE,"E34.MirrorCS")}),1.0]])]});
            var Q8;
            Q8=makeQuery(id+"F0.imprint","IMPRINT",FACE,{"disambiguationData":[TD([[makeQuery(id+"F0.imprint","IMPRINT",EDGE,{"derivedFrom":sQuery(id+"F0.wireOp",EDGE,"E35.MirrorCS")}),1.0]])]});
            var Q9;
            Q9=makeQuery(id+"F0.imprint","IMPRINT",FACE,{"disambiguationData":[TD([[makeQuery(id+"F0.imprint","IMPRINT",EDGE,{"derivedFrom":sQuery(id+"F0.wireOp",EDGE,"E67")}),1.0]])]});
            var Q10;
            Q10=makeQuery(id+"F0.imprint","IMPRINT",FACE,{"disambiguationData":[TD([[makeQuery(id+"F0.imprint","IMPRINT",EDGE,{"derivedFrom":sQuery(id+"F0.wireOp",EDGE,"E49")}),-1.0]])]});
            var Q11;
            Q11=makeQuery(id+"F0.imprint","IMPRINT",FACE,{"disambiguationData":[TD([[makeQuery(id+"F0.imprint","IMPRINT",EDGE,{"derivedFrom":sQuery(id+"F0.wireOp",EDGE,"E27")}),-1.0]])]});
            var Q12;
            Q12=makeQuery(id+"F0.imprint","IMPRINT",FACE,{"disambiguationData":[TD([[makeQuery(id+"F0.imprint","IMPRINT",EDGE,{"derivedFrom":sQuery(id+"F0.wireOp",EDGE,"E16")}),1.0]])]});
            var Q13;
            Q13=makeQuery(id+"F0.imprint","IMPRINT",FACE,{"disambiguationData":[TD([[makeQuery(id+"F0.imprint","IMPRINT",EDGE,{"derivedFrom":sQuery(id+"F0.wireOp",EDGE,"E0")}),1.0]])]});
            extrude(context, id + "F7", {"entities" : qUnion([Q0, Q1, Q2, Q3, Q4, Q5, Q6, Q7, Q8, Q9, Q10, Q11, Q12, Q13]), "depth" : 100 * mm, "offsetDistance" : 25 * mm});
        }
        {
            var Q0;
            Q0=makeQuery(id+"F7.opExtrude","CAP_FACE",FACE,{"disambiguationData":[OSD([sQuery(id+"F0.wireOp",EDGE,"E16"),sQuery(id+"F0.wireOp",EDGE,"E18"),sQuery(id+"F0.wireOp",EDGE,"E20"),sQuery(id+"F0.wireOp",EDGE,"E21"),sQuery(id+"F0.wireOp",EDGE,"E22"),sQuery(id+"F0.wireOp",EDGE,"E23")])],"isStart":false});
            var Q1;
            Q1=makeQuery(id+"F7.opExtrude","CAP_FACE",FACE,{"disambiguationData":[OSD([sQuery(id+"F0.wireOp",EDGE,"E0"),sQuery(id+"F0.wireOp",EDGE,"E41"),sQuery(id+"F0.wireOp",EDGE,"E43"),sQuery(id+"F0.wireOp",EDGE,"E44"),sQuery(id+"F0.wireOp",EDGE,"E45"),sQuery(id+"F0.wireOp",EDGE,"E46")])],"isStart":false});
            var Q2;
            Q2=makeQuery(id+"F7.opExtrude","CAP_FACE",FACE,{"disambiguationData":[OSD([sQuery(id+"F0.wireOp",EDGE,"E49"),sQuery(id+"F0.wireOp",EDGE,"E56"),sQuery(id+"F0.wireOp",EDGE,"E57"),sQuery(id+"F0.wireOp",EDGE,"E62"),sQuery(id+"F0.wireOp",EDGE,"E63"),sQuery(id+"F0.wireOp",EDGE,"E64")])],"isStart":false});
            var Q3;
            Q3=makeQuery(id+"F7.opExtrude","CAP_FACE",FACE,{"disambiguationData":[OSD([sQuery(id+"F0.wireOp",EDGE,"E27"),sQuery(id+"F0.wireOp",EDGE,"E29"),sQuery(id+"F0.wireOp",EDGE,"E54"),sQuery(id+"F0.wireOp",EDGE,"E59"),sQuery(id+"F0.wireOp",EDGE,"E60"),sQuery(id+"F0.wireOp",EDGE,"E61")])],"isStart":false});
            var Q4;
            Q4=makeQuery(id+"F7.opExtrude","CAP_FACE",FACE,{"disambiguationData":[OSD([sQuery(id+"F0.wireOp",EDGE,"E35.MirrorCS"),sQuery(id+"F0.wireOp",EDGE,"E36.MirrorCS"),sQuery(id+"F0.wireOp",EDGE,"E112"),sQuery(id+"F0.wireOp",EDGE,"E114"),sQuery(id+"F0.wireOp",EDGE,"E115"),sQuery(id+"F0.wireOp",EDGE,"E116")])],"isStart":false});
            var Q5;
            Q5=makeQuery(id+"F7.opExtrude","CAP_FACE",FACE,{"disambiguationData":[OSD([sQuery(id+"F0.wireOp",EDGE,"E67"),sQuery(id+"F0.wireOp",EDGE,"E68"),sQuery(id+"F0.wireOp",EDGE,"E109"),sQuery(id+"F0.wireOp",EDGE,"E117"),sQuery(id+"F0.wireOp",EDGE,"E119"),sQuery(id+"F0.wireOp",EDGE,"E120")])],"isStart":false});
            var Q6;
            Q6=makeQuery(id+"F7.opExtrude","CAP_FACE",FACE,{"disambiguationData":[OSD([sQuery(id+"F0.wireOp",EDGE,"E71"),sQuery(id+"F0.wireOp",EDGE,"E72"),sQuery(id+"F0.wireOp",EDGE,"E124"),sQuery(id+"F0.wireOp",EDGE,"E128"),sQuery(id+"F0.wireOp",EDGE,"E129"),sQuery(id+"F0.wireOp",EDGE,"E130")])],"isStart":false});
            var Q7;
            Q7=makeQuery(id+"F7.opExtrude","CAP_FACE",FACE,{"disambiguationData":[OSD([sQuery(id+"F0.wireOp",EDGE,"E34.MirrorCS"),sQuery(id+"F0.wireOp",EDGE,"E87"),sQuery(id+"F0.wireOp",EDGE,"E89"),sQuery(id+"F0.wireOp",EDGE,"E90"),sQuery(id+"F0.wireOp",EDGE,"E91"),sQuery(id+"F0.wireOp",EDGE,"E92")])],"isStart":false});
            var Q8;
            Q8=makeQuery(id+"F7.opExtrude","CAP_FACE",FACE,{"disambiguationData":[OSD([sQuery(id+"F0.wireOp",EDGE,"E94"),sQuery(id+"F0.wireOp",EDGE,"E95"),sQuery(id+"F0.wireOp",EDGE,"E136"),sQuery(id+"F0.wireOp",EDGE,"E138"),sQuery(id+"F0.wireOp",EDGE,"E143"),sQuery(id+"F0.wireOp",EDGE,"E144")])],"isStart":false});
            var Q9;
            Q9=makeQuery(id+"F7.opExtrude","CAP_FACE",FACE,{"disambiguationData":[OSD([sQuery(id+"F0.wireOp",EDGE,"E75"),sQuery(id+"F0.wireOp",EDGE,"E76"),sQuery(id+"F0.wireOp",EDGE,"E131"),sQuery(id+"F0.wireOp",EDGE,"E140"),sQuery(id+"F0.wireOp",EDGE,"E141"),sQuery(id+"F0.wireOp",EDGE,"E142")])],"isStart":false});
            var Q10;
            Q10=makeQuery(id+"F7.opExtrude","CAP_FACE",FACE,{"disambiguationData":[OSD([sQuery(id+"F0.wireOp",EDGE,"E79"),sQuery(id+"F0.wireOp",EDGE,"E80"),sQuery(id+"F0.wireOp",EDGE,"E149"),sQuery(id+"F0.wireOp",EDGE,"E152"),sQuery(id+"F0.wireOp",EDGE,"E153"),sQuery(id+"F0.wireOp",EDGE,"E154")])],"isStart":false});
            var Q11;
            Q11=makeQuery(id+"F7.opExtrude","CAP_FACE",FACE,{"disambiguationData":[OSD([sQuery(id+"F0.wireOp",EDGE,"E98"),sQuery(id+"F0.wireOp",EDGE,"E99"),sQuery(id+"F0.wireOp",EDGE,"E145"),sQuery(id+"F0.wireOp",EDGE,"E156"),sQuery(id+"F0.wireOp",EDGE,"E157"),sQuery(id+"F0.wireOp",EDGE,"E158")])],"isStart":false});
            var Q12;
            Q12=makeQuery(id+"F7.opExtrude","CAP_FACE",FACE,{"disambiguationData":[OSD([sQuery(id+"F0.wireOp",EDGE,"E102"),sQuery(id+"F0.wireOp",EDGE,"E104"),sQuery(id+"F0.wireOp",EDGE,"E159"),sQuery(id+"F0.wireOp",EDGE,"E168"),sQuery(id+"F0.wireOp",EDGE,"E169"),sQuery(id+"F0.wireOp",EDGE,"E170")])],"isStart":false});
            var Q13;
            Q13=makeQuery(id+"F7.opExtrude","CAP_FACE",FACE,{"disambiguationData":[OSD([sQuery(id+"F0.wireOp",EDGE,"E83"),sQuery(id+"F0.wireOp",EDGE,"E84"),sQuery(id+"F0.wireOp",EDGE,"E165"),sQuery(id+"F0.wireOp",EDGE,"E166"),sQuery(id+"F0.wireOp",EDGE,"E171"),sQuery(id+"F0.wireOp",EDGE,"E172")])],"isStart":false});
            var Q14;
            Q14=makeQuery(id+"F7.opExtrude","CAP_FACE",FACE,{"disambiguationData":[OSD([sQuery(id+"F0.wireOp",EDGE,"E83"),sQuery(id+"F0.wireOp",EDGE,"E84"),sQuery(id+"F0.wireOp",EDGE,"E165"),sQuery(id+"F0.wireOp",EDGE,"E166"),sQuery(id+"F0.wireOp",EDGE,"E171"),sQuery(id+"F0.wireOp",EDGE,"E172")])],"isStart":true});
            var Q15;
            Q15=makeQuery(id+"F7.opExtrude","CAP_FACE",FACE,{"disambiguationData":[OSD([sQuery(id+"F0.wireOp",EDGE,"E102"),sQuery(id+"F0.wireOp",EDGE,"E104"),sQuery(id+"F0.wireOp",EDGE,"E159"),sQuery(id+"F0.wireOp",EDGE,"E168"),sQuery(id+"F0.wireOp",EDGE,"E169"),sQuery(id+"F0.wireOp",EDGE,"E170")])],"isStart":true});
            var Q16;
            Q16=makeQuery(id+"F7.opExtrude","CAP_FACE",FACE,{"disambiguationData":[OSD([sQuery(id+"F0.wireOp",EDGE,"E98"),sQuery(id+"F0.wireOp",EDGE,"E99"),sQuery(id+"F0.wireOp",EDGE,"E145"),sQuery(id+"F0.wireOp",EDGE,"E156"),sQuery(id+"F0.wireOp",EDGE,"E157"),sQuery(id+"F0.wireOp",EDGE,"E158")])],"isStart":true});
            var Q17;
            Q17=makeQuery(id+"F7.opExtrude","CAP_FACE",FACE,{"disambiguationData":[OSD([sQuery(id+"F0.wireOp",EDGE,"E79"),sQuery(id+"F0.wireOp",EDGE,"E80"),sQuery(id+"F0.wireOp",EDGE,"E149"),sQuery(id+"F0.wireOp",EDGE,"E152"),sQuery(id+"F0.wireOp",EDGE,"E153"),sQuery(id+"F0.wireOp",EDGE,"E154")])],"isStart":true});
            var Q18;
            Q18=makeQuery(id+"F7.opExtrude","CAP_FACE",FACE,{"disambiguationData":[OSD([sQuery(id+"F0.wireOp",EDGE,"E75"),sQuery(id+"F0.wireOp",EDGE,"E76"),sQuery(id+"F0.wireOp",EDGE,"E131"),sQuery(id+"F0.wireOp",EDGE,"E140"),sQuery(id+"F0.wireOp",EDGE,"E141"),sQuery(id+"F0.wireOp",EDGE,"E142")])],"isStart":true});
            var Q19;
            Q19=makeQuery(id+"F7.opExtrude","CAP_FACE",FACE,{"disambiguationData":[OSD([sQuery(id+"F0.wireOp",EDGE,"E94"),sQuery(id+"F0.wireOp",EDGE,"E95"),sQuery(id+"F0.wireOp",EDGE,"E136"),sQuery(id+"F0.wireOp",EDGE,"E138"),sQuery(id+"F0.wireOp",EDGE,"E143"),sQuery(id+"F0.wireOp",EDGE,"E144")])],"isStart":true});
            var Q20;
            Q20=makeQuery(id+"F7.opExtrude","CAP_FACE",FACE,{"disambiguationData":[OSD([sQuery(id+"F0.wireOp",EDGE,"E71"),sQuery(id+"F0.wireOp",EDGE,"E72"),sQuery(id+"F0.wireOp",EDGE,"E124"),sQuery(id+"F0.wireOp",EDGE,"E128"),sQuery(id+"F0.wireOp",EDGE,"E129"),sQuery(id+"F0.wireOp",EDGE,"E130")])],"isStart":true});
            var Q21;
            Q21=makeQuery(id+"F7.opExtrude","CAP_FACE",FACE,{"disambiguationData":[OSD([sQuery(id+"F0.wireOp",EDGE,"E34.MirrorCS"),sQuery(id+"F0.wireOp",EDGE,"E87"),sQuery(id+"F0.wireOp",EDGE,"E89"),sQuery(id+"F0.wireOp",EDGE,"E90"),sQuery(id+"F0.wireOp",EDGE,"E91"),sQuery(id+"F0.wireOp",EDGE,"E92")])],"isStart":true});
            var Q22;
            Q22=makeQuery(id+"F7.opExtrude","CAP_FACE",FACE,{"disambiguationData":[OSD([sQuery(id+"F0.wireOp",EDGE,"E35.MirrorCS"),sQuery(id+"F0.wireOp",EDGE,"E36.MirrorCS"),sQuery(id+"F0.wireOp",EDGE,"E112"),sQuery(id+"F0.wireOp",EDGE,"E114"),sQuery(id+"F0.wireOp",EDGE,"E115"),sQuery(id+"F0.wireOp",EDGE,"E116")])],"isStart":true});
            var Q23;
            Q23=makeQuery(id+"F7.opExtrude","CAP_FACE",FACE,{"disambiguationData":[OSD([sQuery(id+"F0.wireOp",EDGE,"E67"),sQuery(id+"F0.wireOp",EDGE,"E68"),sQuery(id+"F0.wireOp",EDGE,"E109"),sQuery(id+"F0.wireOp",EDGE,"E117"),sQuery(id+"F0.wireOp",EDGE,"E119"),sQuery(id+"F0.wireOp",EDGE,"E120")])],"isStart":true});
            var Q24;
            Q24=makeQuery(id+"F7.opExtrude","CAP_FACE",FACE,{"disambiguationData":[OSD([sQuery(id+"F0.wireOp",EDGE,"E49"),sQuery(id+"F0.wireOp",EDGE,"E56"),sQuery(id+"F0.wireOp",EDGE,"E57"),sQuery(id+"F0.wireOp",EDGE,"E62"),sQuery(id+"F0.wireOp",EDGE,"E63"),sQuery(id+"F0.wireOp",EDGE,"E64")])],"isStart":true});
            var Q25;
            Q25=makeQuery(id+"F7.opExtrude","CAP_FACE",FACE,{"disambiguationData":[OSD([sQuery(id+"F0.wireOp",EDGE,"E27"),sQuery(id+"F0.wireOp",EDGE,"E29"),sQuery(id+"F0.wireOp",EDGE,"E54"),sQuery(id+"F0.wireOp",EDGE,"E59"),sQuery(id+"F0.wireOp",EDGE,"E60"),sQuery(id+"F0.wireOp",EDGE,"E61")])],"isStart":true});
            var Q26;
            Q26=makeQuery(id+"F7.opExtrude","CAP_FACE",FACE,{"disambiguationData":[OSD([sQuery(id+"F0.wireOp",EDGE,"E16"),sQuery(id+"F0.wireOp",EDGE,"E18"),sQuery(id+"F0.wireOp",EDGE,"E20"),sQuery(id+"F0.wireOp",EDGE,"E21"),sQuery(id+"F0.wireOp",EDGE,"E22"),sQuery(id+"F0.wireOp",EDGE,"E23")])],"isStart":true});
            var Q27;
            Q27=makeQuery(id+"F7.opExtrude","CAP_FACE",FACE,{"disambiguationData":[OSD([sQuery(id+"F0.wireOp",EDGE,"E0"),sQuery(id+"F0.wireOp",EDGE,"E41"),sQuery(id+"F0.wireOp",EDGE,"E43"),sQuery(id+"F0.wireOp",EDGE,"E44"),sQuery(id+"F0.wireOp",EDGE,"E45"),sQuery(id+"F0.wireOp",EDGE,"E46")])],"isStart":true});
            shell(context, id + "F8", {"entities" : qUnion([Q0, Q1, Q2, Q3, Q4, Q5, Q6, Q7, Q8, Q9, Q10, Q11, Q12, Q13, Q14, Q15, Q16, Q17, Q18, Q19, Q20, Q21, Q22, Q23, Q24, Q25, Q26, Q27]), "thickness" : 20 * mm});
        }
        {
            var Q0;
            Q0=sQuery(id+"F0.wireOp",VERTEX,"E175");
            var Q1;
            Q1=sQuery(id+"F0.wireOp",VERTEX,"E176");
            var Q2;
            Q2=sQuery(id+"F0.wireOp",VERTEX,"E177");
            var Q3;
            Q3=sQuery(id+"F0.wireOp",VERTEX,"E178");
            var Q4;
            Q4=sQuery(id+"F0.wireOp",VERTEX,"E179");
            var Q5;
            Q5=sQuery(id+"F0.wireOp",VERTEX,"E180");
            var Q6;
            Q6=sQuery(id+"F0.wireOp",VERTEX,"E181");
            var Q7;
            Q7=sQuery(id+"F0.wireOp",VERTEX,"E182");
            var Q8;
            Q8=sQuery(id+"F0.wireOp",VERTEX,"E183");
            var Q9;
            Q9=sQuery(id+"F0.wireOp",VERTEX,"E184");
            var Q10;
            Q10=sQuery(id+"F0.wireOp",VERTEX,"E185");
            var Q11;
            Q11=sQuery(id+"F0.wireOp",VERTEX,"E186");
            var Q12;
            Q12=sQuery(id+"F0.wireOp",VERTEX,"E187");
            var Q13;
            Q13=sQuery(id+"F0.wireOp",VERTEX,"E188");
            var Q14;
            Q14=makeQuery(id+"F1.opExtrude","SWEPT_BODY",BODY,{"disambiguationData":[OSD([sQuery(id+"F0.wireOp",EDGE,"E40"),sQuery(id+"F0.wireOp",EDGE,"E64"),sQuery(id+"F0.wireOp",EDGE,"E65")])]});
            var Q15;
            Q15=makeQuery(id+"F1.opExtrude","SWEPT_BODY",BODY,{"disambiguationData":[OSD([sQuery(id+"F0.wireOp",EDGE,"E40"),sQuery(id+"F0.wireOp",EDGE,"E66"),sQuery(id+"F0.wireOp",EDGE,"E67")])]});
            var Q16;
            Q16=makeQuery(id+"F1.opExtrude","SWEPT_BODY",BODY,{"disambiguationData":[OSD([sQuery(id+"F0.wireOp",EDGE,"E40"),sQuery(id+"F0.wireOp",EDGE,"E68"),sQuery(id+"F0.wireOp",EDGE,"E69")])]});
            var Q17;
            Q17=makeQuery(id+"F1.opExtrude","SWEPT_BODY",BODY,{"disambiguationData":[OSD([sQuery(id+"F0.wireOp",EDGE,"E40"),sQuery(id+"F0.wireOp",EDGE,"E70"),sQuery(id+"F0.wireOp",EDGE,"E71")])]});
            var Q18;
            Q18=makeQuery(id+"F1.opExtrude","SWEPT_BODY",BODY,{"disambiguationData":[OSD([sQuery(id+"F0.wireOp",EDGE,"E40"),sQuery(id+"F0.wireOp",EDGE,"E72"),sQuery(id+"F0.wireOp",EDGE,"E73")])]});
            var Q19;
            Q19=makeQuery(id+"F1.opExtrude","SWEPT_BODY",BODY,{"disambiguationData":[OSD([sQuery(id+"F0.wireOp",EDGE,"E40"),sQuery(id+"F0.wireOp",EDGE,"E74"),sQuery(id+"F0.wireOp",EDGE,"E75")])]});
            var Q20;
            Q20=makeQuery(id+"F1.opExtrude","SWEPT_BODY",BODY,{"disambiguationData":[OSD([sQuery(id+"F0.wireOp",EDGE,"E40"),sQuery(id+"F0.wireOp",EDGE,"E76"),sQuery(id+"F0.wireOp",EDGE,"E77")])]});
            var Q21;
            Q21=makeQuery(id+"F1.opExtrude","SWEPT_BODY",BODY,{"disambiguationData":[OSD([sQuery(id+"F0.wireOp",EDGE,"E40"),sQuery(id+"F0.wireOp",EDGE,"E78"),sQuery(id+"F0.wireOp",EDGE,"E79")])]});
            var Q22;
            Q22=makeQuery(id+"F1.opExtrude","SWEPT_BODY",BODY,{"disambiguationData":[OSD([sQuery(id+"F0.wireOp",EDGE,"E40"),sQuery(id+"F0.wireOp",EDGE,"E80"),sQuery(id+"F0.wireOp",EDGE,"E81")])]});
            var Q23;
            Q23=makeQuery(id+"F1.opExtrude","SWEPT_BODY",BODY,{"disambiguationData":[OSD([sQuery(id+"F0.wireOp",EDGE,"E40"),sQuery(id+"F0.wireOp",EDGE,"E82"),sQuery(id+"F0.wireOp",EDGE,"E83")])]});
            var Q24;
            Q24=makeQuery(id+"F1.opExtrude","SWEPT_BODY",BODY,{"disambiguationData":[OSD([sQuery(id+"F0.wireOp",EDGE,"E40"),sQuery(id+"F0.wireOp",EDGE,"E84"),sQuery(id+"F0.wireOp",EDGE,"E103")])]});
            hole(context, id + "F9", {"style" : HoleStyle.SIMPLE, "endStyle" : HoleEndStyle.THROUGH, "oppositeDirection" : true, "holeDiameter" : 0.05 * mm, "majorDiameter" : 5 * mm, "isTappedThrough" : true, "tappedDepth" : 12 * mm, "tapClearance" : 3, "startFromSketch" : true, "locations" : qUnion([Q0, Q1, Q2, Q3, Q4, Q5, Q6, Q7, Q8, Q9, Q10, Q11, Q12, Q13]), "scope" : qUnion([Q14, Q15, Q16, Q17, Q18, Q19, Q20, Q21, Q22, Q23, Q24])});
        }
    });
